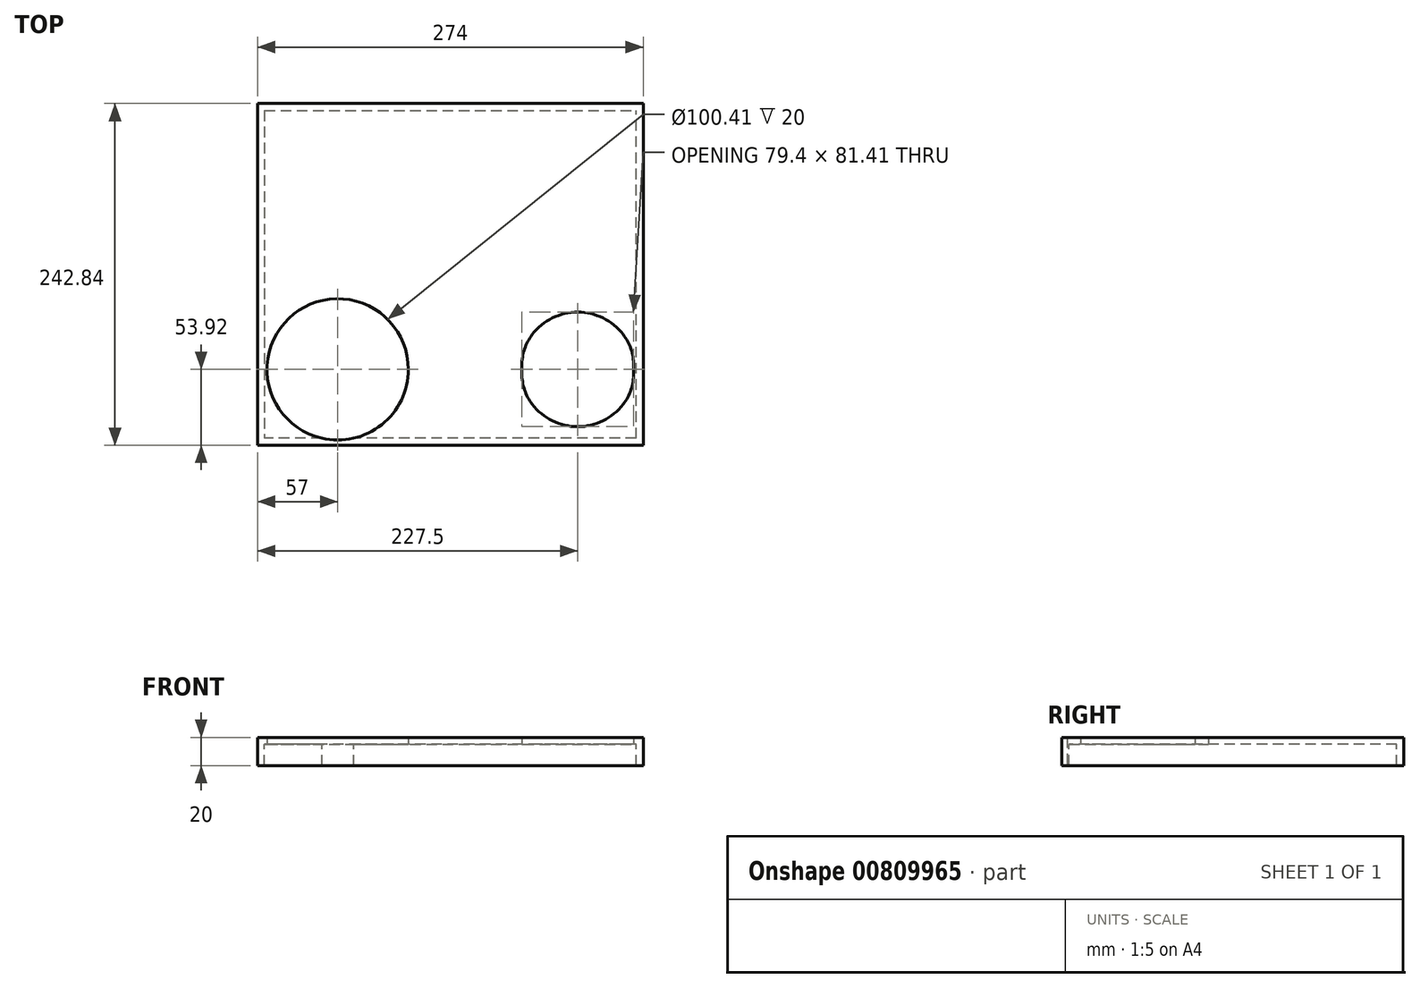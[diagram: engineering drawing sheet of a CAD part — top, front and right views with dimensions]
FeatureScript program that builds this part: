
annotation { "Feature Type Name" : "Feature", "Feature Type Description" : "" }
export const myFeature = defineFeature(function(context is Context, id is Id, definition is map)
    precondition{}
    {
        {
            var Q0;
            Q0=qCreatedBy(makeId("Top.planeOp"),FACE);
            var sketch = newSketch(context, id + "F0", { "sketchPlane" : qUnion([Q0])});
            skLineSegment(sketch, "E0", {"start": v(-69.05, 97.42) * mm, "end": v(-68.86, 97) * mm});
            skLineSegment(sketch, "E1", {"start": v(-70.25, 100) * mm, "end": v(-69.05, 97.42) * mm});
            skLineSegment(sketch, "E2", {"start": v(-70.71, 101) * mm, "end": v(-70.25, 100) * mm});
            skLineSegment(sketch, "E3", {"start": v(-75.98, 112.53) * mm, "end": v(-70.72, 101) * mm});
            skLineSegment(sketch, "E4", {"start": v(-75.97, 112.51) * mm, "end": v(-65.07, 114.65) * mm});
            skLineSegment(sketch, "E5", {"start": v(-65.07, 114.67) * mm, "end": v(-64.3, 114.83) * mm});
            skArc(sketch, "E6", {"start": v(-64.11, 114.85) * mm, "mid": v(-64.2, 114.84) * mm, "end": v(-64.3, 114.83) * mm});
            skLineSegment(sketch, "E7", {"start": v(-64.11, 114.85) * mm, "end": v(-62.9, 114.9) * mm});
            skLineSegment(sketch, "E8", {"start": v(139.49, -112.35) * mm, "end": v(140.85, -114.93) * mm});
            skLineSegment(sketch, "E9", {"start": v(139.48, -114.72) * mm, "end": v(140.85, -114.93) * mm});
            skLineSegment(sketch, "E10", {"start": v(130, -97.08) * mm, "end": v(130.29, -97.1) * mm});
            skLineSegment(sketch, "E11", {"start": v(130.29, -97.1) * mm, "end": v(131.36, -97) * mm});
            skLineSegment(sketch, "E12", {"start": v(131.36, -97.01) * mm, "end": v(132.95, -100) * mm});
            skLineSegment(sketch, "E13", {"start": v(132.95, -100) * mm, "end": v(133.48, -101) * mm});
            skLineSegment(sketch, "E14", {"start": v(133.48, -101) * mm, "end": v(139.49, -112.35) * mm});
            skLineSegment(sketch, "E15", {"start": v(136.64, -109.43) * mm, "end": v(139.48, -114.72) * mm});
            skLineSegment(sketch, "E16", {"start": v(139.48, -114.72) * mm, "end": v(-60.98, -114.72) * mm});
            skLineSegment(sketch, "E17", {"start": v(-51.5, -97.08) * mm, "end": v(130, -97.08) * mm});
            skLineSegment(sketch, "E18", {"start": v(130, -97.08) * mm, "end": v(131.57, -100) * mm});
            skLineSegment(sketch, "E19", {"start": v(131.57, -100) * mm, "end": v(132.1, -101) * mm});
            skLineSegment(sketch, "E20", {"start": v(132.1, -101) * mm, "end": v(136.64, -109.43) * mm});
            skLineSegment(sketch, "E21", {"start": v(-60.98, -114.72) * mm, "end": v(-58.14, -109.43) * mm});
            skLineSegment(sketch, "E22", {"start": v(-62.35, -114.94) * mm, "end": v(-60.98, -114.72) * mm});
            skLineSegment(sketch, "E23", {"start": v(-52.86, -97) * mm, "end": v(-51.79, -97.1) * mm});
            skLineSegment(sketch, "E24", {"start": v(-51.79, -97.1) * mm, "end": v(-51.5, -97.08) * mm});
            skLineSegment(sketch, "E25", {"start": v(-53.07, -100) * mm, "end": v(-51.5, -97.08) * mm});
            skLineSegment(sketch, "E26", {"start": v(-53.6, -101) * mm, "end": v(-53.07, -100) * mm});
            skLineSegment(sketch, "E27", {"start": v(-58.14, -109.43) * mm, "end": v(-53.6, -101) * mm});
            skLineSegment(sketch, "E28", {"start": v(-62.35, -114.93) * mm, "end": v(-60.99, -112.35) * mm});
            skLineSegment(sketch, "E29", {"start": v(-75.98, -112.53) * mm, "end": v(-70.72, -101) * mm});
            skLineSegment(sketch, "E30", {"start": v(-70.71, -101) * mm, "end": v(-70.25, -100) * mm});
            skLineSegment(sketch, "E31", {"start": v(-70.25, -100) * mm, "end": v(-69.05, -97.42) * mm});
            skLineSegment(sketch, "E32", {"start": v(-69.05, -97.42) * mm, "end": v(-68.86, -97) * mm});
            skLineSegment(sketch, "E33", {"start": v(-68.86, -97) * mm, "end": v(-68.39, -96) * mm});
            skLineSegment(sketch, "E34", {"start": v(-68.39, -96) * mm, "end": v(-67.71, -94.55) * mm});
            skLineSegment(sketch, "E35", {"start": v(-67.71, -94.56) * mm, "end": v(-59.49, -96.01) * mm});
            skLineSegment(sketch, "E36", {"start": v(-59.49, -96) * mm, "end": v(-56.67, -96.45) * mm});
            skLineSegment(sketch, "E37", {"start": v(-56.67, -96.46) * mm, "end": v(-52.94, -97) * mm});
            skLineSegment(sketch, "E38", {"start": v(-52.94, -97) * mm, "end": v(-52.86, -97.01) * mm});
            skLineSegment(sketch, "E39", {"start": v(-54.45, -100) * mm, "end": v(-52.86, -97.01) * mm});
            skLineSegment(sketch, "E40", {"start": v(-54.98, -101) * mm, "end": v(-54.45, -100) * mm});
            skLineSegment(sketch, "E41", {"start": v(-60.99, -112.35) * mm, "end": v(-54.98, -101) * mm});
            skLineSegment(sketch, "E42", {"start": v(-62.9, -114.9) * mm, "end": v(-62.35, -114.93) * mm});
            skLineSegment(sketch, "E43", {"start": v(-64.53, -115.5) * mm, "end": v(-62.85, -115.56) * mm});
            skLineSegment(sketch, "E44", {"start": v(-64.11, -114.85) * mm, "end": v(-62.9, -114.9) * mm});
            skArc(sketch, "E45", {"start": v(-64.88, -115.47) * mm, "mid": v(-64.7, -115.5) * mm, "end": v(-64.53, -115.5) * mm});
            skArc(sketch, "E46", {"start": v(-64.3, -114.83) * mm, "mid": v(-64.2, -114.84) * mm, "end": v(-64.11, -114.85) * mm});
            skLineSegment(sketch, "E47", {"start": v(-75.97, -112.51) * mm, "end": v(-65.07, -114.65) * mm});
            skLineSegment(sketch, "E48", {"start": v(-65.07, -114.67) * mm, "end": v(-64.3, -114.83) * mm});
            skLineSegment(sketch, "E49", {"start": v(-64.9, -115.47) * mm, "end": v(-64.88, -115.47) * mm});
            skLineSegment(sketch, "E50", {"start": v(-64.88, -115.47) * mm, "end": v(-64.92, -115.97) * mm});
            skLineSegment(sketch, "E51", {"start": v(-91.1, -111.35) * mm, "end": v(-64.92, -115.97) * mm});
            skLineSegment(sketch, "E52", {"start": v(-91.1, -111.35) * mm, "end": v(-90.57, -110.91) * mm});
            skLineSegment(sketch, "E53", {"start": v(-76.02, -113.37) * mm, "end": v(-66.82, -115.07) * mm});
            skLineSegment(sketch, "E54", {"start": v(-66.82, -115.08) * mm, "end": v(-64.9, -115.47) * mm});
            skLineSegment(sketch, "E55", {"start": v(157.61, -91.65) * mm, "end": v(130.3, -96.47) * mm});
            skLineSegment(sketch, "E56", {"start": v(130.3, -96.47) * mm, "end": v(-51.8, -96.47) * mm});
            skLineSegment(sketch, "E57", {"start": v(-51.8, -96.47) * mm, "end": v(-79.11, -91.65) * mm});
            skLineSegment(sketch, "E58", {"start": v(-79.53, -91.16) * mm, "end": v(-79.52, -91.23) * mm});
            skLineSegment(sketch, "E59", {"start": v(-79.52, -91.23) * mm, "end": v(-79.5, -91.3) * mm});
            skLineSegment(sketch, "E60", {"start": v(-79.5, -91.3) * mm, "end": v(-79.48, -91.37) * mm});
            skLineSegment(sketch, "E61", {"start": v(-79.48, -91.37) * mm, "end": v(-79.45, -91.43) * mm});
            skLineSegment(sketch, "E62", {"start": v(-79.45, -91.43) * mm, "end": v(-79.41, -91.48) * mm});
            skLineSegment(sketch, "E63", {"start": v(-79.41, -91.48) * mm, "end": v(-79.36, -91.53) * mm});
            skLineSegment(sketch, "E64", {"start": v(-79.36, -91.53) * mm, "end": v(-79.3, -91.58) * mm});
            skLineSegment(sketch, "E65", {"start": v(-79.3, -91.58) * mm, "end": v(-79.25, -91.61) * mm});
            skLineSegment(sketch, "E66", {"start": v(-79.25, -91.61) * mm, "end": v(-79.18, -91.64) * mm});
            skLineSegment(sketch, "E67", {"start": v(-79.18, -91.64) * mm, "end": v(-79.11, -91.65) * mm});
            skLineSegment(sketch, "E68", {"start": v(-79.53, -91.16) * mm, "end": v(-79.53, 91.16) * mm});
            skEllipticalArc(sketch, "E69", {});
            skLineSegment(sketch, "E70", {"start": v(-79.11, 91.65) * mm, "end": v(-51.8, 96.47) * mm});
            skLineSegment(sketch, "E71", {"start": v(-51.8, 96.47) * mm, "end": v(130.3, 96.47) * mm});
            skLineSegment(sketch, "E72", {"start": v(130.3, 96.47) * mm, "end": v(157.61, 91.65) * mm});
            skLineSegment(sketch, "E73", {"start": v(158.03, 91.16) * mm, "end": v(158.02, 91.23) * mm});
            skLineSegment(sketch, "E74", {"start": v(158.02, 91.23) * mm, "end": v(158, 91.3) * mm});
            skLineSegment(sketch, "E75", {"start": v(158, 91.3) * mm, "end": v(157.98, 91.37) * mm});
            skLineSegment(sketch, "E76", {"start": v(157.98, 91.37) * mm, "end": v(157.95, 91.43) * mm});
            skLineSegment(sketch, "E77", {"start": v(157.95, 91.43) * mm, "end": v(157.91, 91.48) * mm});
            skLineSegment(sketch, "E78", {"start": v(157.91, 91.48) * mm, "end": v(157.86, 91.53) * mm});
            skLineSegment(sketch, "E79", {"start": v(157.86, 91.53) * mm, "end": v(157.8, 91.58) * mm});
            skLineSegment(sketch, "E80", {"start": v(157.8, 91.58) * mm, "end": v(157.75, 91.61) * mm});
            skLineSegment(sketch, "E81", {"start": v(157.75, 91.61) * mm, "end": v(157.68, 91.64) * mm});
            skLineSegment(sketch, "E82", {"start": v(157.68, 91.64) * mm, "end": v(157.61, 91.65) * mm});
            skLineSegment(sketch, "E83", {"start": v(158.03, 91.16) * mm, "end": v(158.03, -91.16) * mm});
            skLineSegment(sketch, "E84", {"start": v(157.61, -91.65) * mm, "end": v(157.68, -91.64) * mm});
            skLineSegment(sketch, "E85", {"start": v(157.68, -91.64) * mm, "end": v(157.75, -91.61) * mm});
            skLineSegment(sketch, "E86", {"start": v(157.75, -91.61) * mm, "end": v(157.8, -91.58) * mm});
            skLineSegment(sketch, "E87", {"start": v(157.8, -91.58) * mm, "end": v(157.86, -91.53) * mm});
            skLineSegment(sketch, "E88", {"start": v(157.86, -91.53) * mm, "end": v(157.91, -91.48) * mm});
            skLineSegment(sketch, "E89", {"start": v(157.91, -91.48) * mm, "end": v(157.95, -91.43) * mm});
            skLineSegment(sketch, "E90", {"start": v(157.95, -91.43) * mm, "end": v(157.98, -91.37) * mm});
            skLineSegment(sketch, "E91", {"start": v(157.98, -91.37) * mm, "end": v(158, -91.3) * mm});
            skLineSegment(sketch, "E92", {"start": v(158, -91.3) * mm, "end": v(158.02, -91.23) * mm});
            skLineSegment(sketch, "E93", {"start": v(158.02, -91.23) * mm, "end": v(158.03, -91.16) * mm});
            skLineSegment(sketch, "E94", {"start": v(169.07, -110.91) * mm, "end": v(169.09, -110.9) * mm});
            skLineSegment(sketch, "E95", {"start": v(169.09, -110.9) * mm, "end": v(169.1, -110.86) * mm});
            skLineSegment(sketch, "E96", {"start": v(169.1, -110.86) * mm, "end": v(169.1, -110.8) * mm});
            skLineSegment(sketch, "E97", {"start": v(169.1, -110.8) * mm, "end": v(169.1, -110.73) * mm});
            skLineSegment(sketch, "E98", {"start": v(169.1, -110.73) * mm, "end": v(169.1, -110.64) * mm});
            skLineSegment(sketch, "E99", {"start": v(169.1, -110.64) * mm, "end": v(169.1, -110.54) * mm});
            skLineSegment(sketch, "E100", {"start": v(169.1, -110.54) * mm, "end": v(169.1, -110.43) * mm});
            skLineSegment(sketch, "E101", {"start": v(169.1, -110.43) * mm, "end": v(169.08, -110.31) * mm});
            skLineSegment(sketch, "E102", {"start": v(169.08, -110.31) * mm, "end": v(169.06, -110.18) * mm});
            skLineSegment(sketch, "E103", {"start": v(169.06, -110.18) * mm, "end": v(169.04, -110.05) * mm});
            skEllipticalArc(sketch, "E104", {});
            skLineSegment(sketch, "E105", {"start": v(142.98, -115.5) * mm, "end": v(143.03, -115.5) * mm});
            skLineSegment(sketch, "E106", {"start": v(142.61, -114.85) * mm, "end": v(142.64, -114.97) * mm});
            skLineSegment(sketch, "E107", {"start": v(142.64, -114.97) * mm, "end": v(142.67, -115.09) * mm});
            skLineSegment(sketch, "E108", {"start": v(142.67, -115.09) * mm, "end": v(142.71, -115.19) * mm});
            skLineSegment(sketch, "E109", {"start": v(142.71, -115.19) * mm, "end": v(142.76, -115.28) * mm});
            skLineSegment(sketch, "E110", {"start": v(142.76, -115.28) * mm, "end": v(142.8, -115.36) * mm});
            skLineSegment(sketch, "E111", {"start": v(142.8, -115.36) * mm, "end": v(142.86, -115.42) * mm});
            skLineSegment(sketch, "E112", {"start": v(142.86, -115.42) * mm, "end": v(142.92, -115.47) * mm});
            skLineSegment(sketch, "E113", {"start": v(142.92, -115.47) * mm, "end": v(142.98, -115.5) * mm});
            skEllipticalArc(sketch, "E114", {});
            skLineSegment(sketch, "E115", {"start": v(140.85, -114.93) * mm, "end": v(140.89, -115.06) * mm});
            skLineSegment(sketch, "E116", {"start": v(140.89, -115.06) * mm, "end": v(140.93, -115.18) * mm});
            skLineSegment(sketch, "E117", {"start": v(140.93, -115.18) * mm, "end": v(140.99, -115.28) * mm});
            skLineSegment(sketch, "E118", {"start": v(140.99, -115.28) * mm, "end": v(141.05, -115.37) * mm});
            skLineSegment(sketch, "E119", {"start": v(141.05, -115.37) * mm, "end": v(141.12, -115.45) * mm});
            skLineSegment(sketch, "E120", {"start": v(141.12, -115.45) * mm, "end": v(141.2, -115.5) * mm});
            skLineSegment(sketch, "E121", {"start": v(141.2, -115.5) * mm, "end": v(141.27, -115.54) * mm});
            skLineSegment(sketch, "E122", {"start": v(141.27, -115.54) * mm, "end": v(141.35, -115.56) * mm});
            skLineSegment(sketch, "E123", {"start": v(169.04, 110.05) * mm, "end": v(169.06, 110.18) * mm});
            skLineSegment(sketch, "E124", {"start": v(169.06, 110.18) * mm, "end": v(169.08, 110.31) * mm});
            skLineSegment(sketch, "E125", {"start": v(169.08, 110.31) * mm, "end": v(169.1, 110.43) * mm});
            skLineSegment(sketch, "E126", {"start": v(169.1, 110.43) * mm, "end": v(169.1, 110.54) * mm});
            skLineSegment(sketch, "E127", {"start": v(169.1, 110.54) * mm, "end": v(169.1, 110.64) * mm});
            skLineSegment(sketch, "E128", {"start": v(169.1, 110.64) * mm, "end": v(169.1, 110.73) * mm});
            skLineSegment(sketch, "E129", {"start": v(169.1, 110.73) * mm, "end": v(169.1, 110.8) * mm});
            skLineSegment(sketch, "E130", {"start": v(169.1, 110.8) * mm, "end": v(169.1, 110.86) * mm});
            skLineSegment(sketch, "E131", {"start": v(169.1, 110.86) * mm, "end": v(169.09, 110.9) * mm});
            skLineSegment(sketch, "E132", {"start": v(169.09, 110.9) * mm, "end": v(169.07, 110.91) * mm});
            skLineSegment(sketch, "E133", {"start": v(139.48, -114.72) * mm, "end": v(139.48, -115.59) * mm});
            skLineSegment(sketch, "E134", {"start": v(-60.98, -114.72) * mm, "end": v(-60.98, -115.59) * mm});
            skEllipticalArc(sketch, "E135", {});
            skEllipticalArc(sketch, "E136", {});
            skEllipticalArc(sketch, "E137", {});
            skLineSegment(sketch, "E138", {"start": v(139.48, 115.59) * mm, "end": v(139.48, 114.72) * mm});
            skLineSegment(sketch, "E139", {"start": v(-60.98, 115.59) * mm, "end": v(-60.98, 114.72) * mm});
            skLineSegment(sketch, "E140", {"start": v(-90.54, -110.05) * mm, "end": v(-90.56, -110.18) * mm});
            skLineSegment(sketch, "E141", {"start": v(-90.56, -110.18) * mm, "end": v(-90.58, -110.31) * mm});
            skLineSegment(sketch, "E142", {"start": v(-90.58, -110.31) * mm, "end": v(-90.6, -110.43) * mm});
            skLineSegment(sketch, "E143", {"start": v(-90.6, -110.43) * mm, "end": v(-90.6, -110.54) * mm});
            skLineSegment(sketch, "E144", {"start": v(-90.6, -110.54) * mm, "end": v(-90.6, -110.64) * mm});
            skLineSegment(sketch, "E145", {"start": v(-90.6, -110.64) * mm, "end": v(-90.6, -110.73) * mm});
            skLineSegment(sketch, "E146", {"start": v(-90.6, -110.73) * mm, "end": v(-90.6, -110.8) * mm});
            skLineSegment(sketch, "E147", {"start": v(-90.6, -110.8) * mm, "end": v(-90.6, -110.86) * mm});
            skLineSegment(sketch, "E148", {"start": v(-90.6, -110.86) * mm, "end": v(-90.59, -110.9) * mm});
            skLineSegment(sketch, "E149", {"start": v(-90.59, -110.9) * mm, "end": v(-90.57, -110.91) * mm});
            skLineSegment(sketch, "E150", {"start": v(-92.22, -108.95) * mm, "end": v(-92.2, -108.96) * mm});
            skLineSegment(sketch, "E151", {"start": v(-92.2, -108.96) * mm, "end": v(-92.17, -108.98) * mm});
            skLineSegment(sketch, "E152", {"start": v(-92.17, -108.98) * mm, "end": v(-92.12, -109) * mm});
            skLineSegment(sketch, "E153", {"start": v(-92.12, -109) * mm, "end": v(-92.05, -109.01) * mm});
            skLineSegment(sketch, "E154", {"start": v(-92.05, -109.01) * mm, "end": v(-91.96, -109.02) * mm});
            skLineSegment(sketch, "E155", {"start": v(-91.96, -109.02) * mm, "end": v(-91.87, -109.04) * mm});
            skLineSegment(sketch, "E156", {"start": v(-91.87, -109.04) * mm, "end": v(-91.75, -109.05) * mm});
            skLineSegment(sketch, "E157", {"start": v(-91.75, -109.05) * mm, "end": v(-91.63, -109.06) * mm});
            skLineSegment(sketch, "E158", {"start": v(-91.63, -109.06) * mm, "end": v(-91.5, -109.06) * mm});
            skLineSegment(sketch, "E159", {"start": v(-91.5, -109.06) * mm, "end": v(-91.37, -109.07) * mm});
            skEllipticalArc(sketch, "E160", {});
            skEllipticalArc(sketch, "E161", {});
            skLineSegment(sketch, "E162", {"start": v(158.4, -92.33) * mm, "end": v(158.39, -92.26) * mm});
            skLineSegment(sketch, "E163", {"start": v(158.39, -92.26) * mm, "end": v(158.38, -92.2) * mm});
            skLineSegment(sketch, "E164", {"start": v(158.38, -92.2) * mm, "end": v(158.36, -92.13) * mm});
            skLineSegment(sketch, "E165", {"start": v(158.36, -92.13) * mm, "end": v(158.35, -92.06) * mm});
            skLineSegment(sketch, "E166", {"start": v(158.35, -92.06) * mm, "end": v(158.33, -92) * mm});
            skLineSegment(sketch, "E167", {"start": v(158.33, -92) * mm, "end": v(158.32, -91.95) * mm});
            skLineSegment(sketch, "E168", {"start": v(158.32, -91.95) * mm, "end": v(158.3, -91.9) * mm});
            skLineSegment(sketch, "E169", {"start": v(158.3, -91.9) * mm, "end": v(158.3, -91.86) * mm});
            skLineSegment(sketch, "E170", {"start": v(158.3, -91.86) * mm, "end": v(158.28, -91.83) * mm});
            skLineSegment(sketch, "E171", {"start": v(158.28, -91.83) * mm, "end": v(158.27, -91.8) * mm});
            skLineSegment(sketch, "E172", {"start": v(158.27, -91.8) * mm, "end": v(158.26, -91.79) * mm});
            skLineSegment(sketch, "E173", {"start": v(158.26, -91.79) * mm, "end": v(158.25, -91.78) * mm});
            skLineSegment(sketch, "E174", {"start": v(158.67, -91.3) * mm, "end": v(158.68, -91.3) * mm});
            skLineSegment(sketch, "E175", {"start": v(158.68, -91.3) * mm, "end": v(158.7, -91.3) * mm});
            skLineSegment(sketch, "E176", {"start": v(158.7, -91.3) * mm, "end": v(158.74, -91.31) * mm});
            skLineSegment(sketch, "E177", {"start": v(158.74, -91.31) * mm, "end": v(158.78, -91.32) * mm});
            skLineSegment(sketch, "E178", {"start": v(158.78, -91.32) * mm, "end": v(158.83, -91.33) * mm});
            skLineSegment(sketch, "E179", {"start": v(158.83, -91.33) * mm, "end": v(158.89, -91.33) * mm});
            skLineSegment(sketch, "E180", {"start": v(158.89, -91.33) * mm, "end": v(158.95, -91.34) * mm});
            skLineSegment(sketch, "E181", {"start": v(158.95, -91.34) * mm, "end": v(159.02, -91.34) * mm});
            skLineSegment(sketch, "E182", {"start": v(159.02, -91.34) * mm, "end": v(159.09, -91.34) * mm});
            skLineSegment(sketch, "E183", {"start": v(159.09, -91.34) * mm, "end": v(159.16, -91.34) * mm});
            skLineSegment(sketch, "E184", {"start": v(159.16, -91.34) * mm, "end": v(159.23, -91.34) * mm});
            skEllipticalArc(sketch, "E185", {});
            skLineSegment(sketch, "E186", {"start": v(158.25, 91.78) * mm, "end": v(158.26, 91.79) * mm});
            skLineSegment(sketch, "E187", {"start": v(158.26, 91.79) * mm, "end": v(158.27, 91.8) * mm});
            skLineSegment(sketch, "E188", {"start": v(158.27, 91.8) * mm, "end": v(158.28, 91.83) * mm});
            skLineSegment(sketch, "E189", {"start": v(158.28, 91.83) * mm, "end": v(158.3, 91.86) * mm});
            skLineSegment(sketch, "E190", {"start": v(158.3, 91.86) * mm, "end": v(158.3, 91.9) * mm});
            skLineSegment(sketch, "E191", {"start": v(158.3, 91.9) * mm, "end": v(158.32, 91.95) * mm});
            skLineSegment(sketch, "E192", {"start": v(158.32, 91.95) * mm, "end": v(158.33, 92) * mm});
            skLineSegment(sketch, "E193", {"start": v(158.33, 92) * mm, "end": v(158.35, 92.06) * mm});
            skLineSegment(sketch, "E194", {"start": v(158.35, 92.06) * mm, "end": v(158.36, 92.13) * mm});
            skLineSegment(sketch, "E195", {"start": v(158.36, 92.13) * mm, "end": v(158.38, 92.2) * mm});
            skLineSegment(sketch, "E196", {"start": v(158.38, 92.2) * mm, "end": v(158.39, 92.26) * mm});
            skLineSegment(sketch, "E197", {"start": v(158.39, 92.26) * mm, "end": v(158.4, 92.33) * mm});
            skLineSegment(sketch, "E198", {"start": v(-79.75, -91.78) * mm, "end": v(-79.76, -91.79) * mm});
            skLineSegment(sketch, "E199", {"start": v(-79.76, -91.79) * mm, "end": v(-79.77, -91.8) * mm});
            skLineSegment(sketch, "E200", {"start": v(-79.77, -91.8) * mm, "end": v(-79.78, -91.83) * mm});
            skLineSegment(sketch, "E201", {"start": v(-79.78, -91.83) * mm, "end": v(-79.8, -91.86) * mm});
            skLineSegment(sketch, "E202", {"start": v(-79.8, -91.86) * mm, "end": v(-79.8, -91.9) * mm});
            skLineSegment(sketch, "E203", {"start": v(-79.8, -91.9) * mm, "end": v(-79.82, -91.95) * mm});
            skLineSegment(sketch, "E204", {"start": v(-79.82, -91.95) * mm, "end": v(-79.83, -92) * mm});
            skLineSegment(sketch, "E205", {"start": v(-79.83, -92) * mm, "end": v(-79.85, -92.06) * mm});
            skLineSegment(sketch, "E206", {"start": v(-79.85, -92.06) * mm, "end": v(-79.86, -92.13) * mm});
            skLineSegment(sketch, "E207", {"start": v(-79.86, -92.13) * mm, "end": v(-79.88, -92.2) * mm});
            skLineSegment(sketch, "E208", {"start": v(-79.88, -92.2) * mm, "end": v(-79.89, -92.26) * mm});
            skLineSegment(sketch, "E209", {"start": v(-79.89, -92.26) * mm, "end": v(-79.9, -92.33) * mm});
            skLineSegment(sketch, "E210", {"start": v(-80.73, -91.34) * mm, "end": v(-80.66, -91.34) * mm});
            skLineSegment(sketch, "E211", {"start": v(-80.66, -91.34) * mm, "end": v(-80.59, -91.34) * mm});
            skLineSegment(sketch, "E212", {"start": v(-80.59, -91.34) * mm, "end": v(-80.52, -91.34) * mm});
            skLineSegment(sketch, "E213", {"start": v(-80.52, -91.34) * mm, "end": v(-80.45, -91.34) * mm});
            skLineSegment(sketch, "E214", {"start": v(-80.45, -91.34) * mm, "end": v(-80.39, -91.33) * mm});
            skLineSegment(sketch, "E215", {"start": v(-80.39, -91.33) * mm, "end": v(-80.33, -91.33) * mm});
            skLineSegment(sketch, "E216", {"start": v(-80.33, -91.33) * mm, "end": v(-80.28, -91.32) * mm});
            skLineSegment(sketch, "E217", {"start": v(-80.28, -91.32) * mm, "end": v(-80.24, -91.31) * mm});
            skLineSegment(sketch, "E218", {"start": v(-80.24, -91.31) * mm, "end": v(-80.2, -91.3) * mm});
            skLineSegment(sketch, "E219", {"start": v(-80.2, -91.3) * mm, "end": v(-80.18, -91.3) * mm});
            skLineSegment(sketch, "E220", {"start": v(-80.18, -91.3) * mm, "end": v(-80.17, -91.3) * mm});
            skLineSegment(sketch, "E221", {"start": v(-80.17, 91.3) * mm, "end": v(-80.18, 91.3) * mm});
            skLineSegment(sketch, "E222", {"start": v(-80.18, 91.3) * mm, "end": v(-80.2, 91.3) * mm});
            skLineSegment(sketch, "E223", {"start": v(-80.2, 91.3) * mm, "end": v(-80.24, 91.31) * mm});
            skLineSegment(sketch, "E224", {"start": v(-80.24, 91.31) * mm, "end": v(-80.28, 91.32) * mm});
            skLineSegment(sketch, "E225", {"start": v(-80.28, 91.32) * mm, "end": v(-80.33, 91.33) * mm});
            skLineSegment(sketch, "E226", {"start": v(-80.33, 91.33) * mm, "end": v(-80.39, 91.33) * mm});
            skLineSegment(sketch, "E227", {"start": v(-80.39, 91.33) * mm, "end": v(-80.45, 91.34) * mm});
            skLineSegment(sketch, "E228", {"start": v(-80.45, 91.34) * mm, "end": v(-80.52, 91.34) * mm});
            skLineSegment(sketch, "E229", {"start": v(-80.52, 91.34) * mm, "end": v(-80.59, 91.34) * mm});
            skLineSegment(sketch, "E230", {"start": v(-80.59, 91.34) * mm, "end": v(-80.66, 91.34) * mm});
            skLineSegment(sketch, "E231", {"start": v(-80.66, 91.34) * mm, "end": v(-80.73, 91.34) * mm});
            skLineSegment(sketch, "E232", {"start": v(-79.9, 92.33) * mm, "end": v(-79.89, 92.26) * mm});
            skLineSegment(sketch, "E233", {"start": v(-79.89, 92.26) * mm, "end": v(-79.88, 92.2) * mm});
            skLineSegment(sketch, "E234", {"start": v(-79.88, 92.2) * mm, "end": v(-79.86, 92.13) * mm});
            skLineSegment(sketch, "E235", {"start": v(-79.86, 92.13) * mm, "end": v(-79.85, 92.06) * mm});
            skLineSegment(sketch, "E236", {"start": v(-79.85, 92.06) * mm, "end": v(-79.83, 92) * mm});
            skLineSegment(sketch, "E237", {"start": v(-79.83, 92) * mm, "end": v(-79.82, 91.95) * mm});
            skLineSegment(sketch, "E238", {"start": v(-79.82, 91.95) * mm, "end": v(-79.8, 91.9) * mm});
            skLineSegment(sketch, "E239", {"start": v(-79.8, 91.9) * mm, "end": v(-79.8, 91.86) * mm});
            skLineSegment(sketch, "E240", {"start": v(-79.8, 91.86) * mm, "end": v(-79.78, 91.83) * mm});
            skLineSegment(sketch, "E241", {"start": v(-79.78, 91.83) * mm, "end": v(-79.77, 91.8) * mm});
            skLineSegment(sketch, "E242", {"start": v(-79.77, 91.8) * mm, "end": v(-79.76, 91.79) * mm});
            skLineSegment(sketch, "E243", {"start": v(-79.76, 91.79) * mm, "end": v(-79.75, 91.78) * mm});
            skLineSegment(sketch, "E244", {"start": v(-51.5, -96.52) * mm, "end": v(-51.5, -97) * mm});
            skLineSegment(sketch, "E245", {"start": v(-51.5, -97) * mm, "end": v(-51.5, -97.08) * mm});
            skLineSegment(sketch, "E246", {"start": v(130, -96.52) * mm, "end": v(130, -97) * mm});
            skLineSegment(sketch, "E247", {"start": v(130, -97) * mm, "end": v(130, -97.08) * mm});
            skLineSegment(sketch, "E248", {"start": v(130, 97.08) * mm, "end": v(130, 97) * mm});
            skLineSegment(sketch, "E249", {"start": v(130, 97) * mm, "end": v(130, 96.52) * mm});
            skLineSegment(sketch, "E250", {"start": v(-51.5, 97) * mm, "end": v(-51.5, 96.52) * mm});
            skLineSegment(sketch, "E251", {"start": v(-51.5, 97.08) * mm, "end": v(-51.5, 97) * mm});
            skEllipticalArc(sketch, "E252", {});
            skEllipticalArc(sketch, "E253", {});
            skLineSegment(sketch, "E254", {"start": v(-90.54, 110.05) * mm, "end": v(-75.97, 112.53) * mm});
            skLineSegment(sketch, "E255", {"start": v(-67.71, 94.55) * mm, "end": v(-79.9, 92.33) * mm});
            skEllipticalArc(sketch, "E256", {});
            skEllipticalArc(sketch, "E257", {});
            skLineSegment(sketch, "E258", {"start": v(146.21, -94.55) * mm, "end": v(146.2, -94.48) * mm});
            skLineSegment(sketch, "E259", {"start": v(146.2, -94.48) * mm, "end": v(146.19, -94.41) * mm});
            skLineSegment(sketch, "E260", {"start": v(146.19, -94.41) * mm, "end": v(146.17, -94.35) * mm});
            skLineSegment(sketch, "E261", {"start": v(146.17, -94.35) * mm, "end": v(146.16, -94.28) * mm});
            skLineSegment(sketch, "E262", {"start": v(146.16, -94.28) * mm, "end": v(146.14, -94.22) * mm});
            skLineSegment(sketch, "E263", {"start": v(146.14, -94.22) * mm, "end": v(146.13, -94.17) * mm});
            skLineSegment(sketch, "E264", {"start": v(146.13, -94.17) * mm, "end": v(146.12, -94.12) * mm});
            skLineSegment(sketch, "E265", {"start": v(146.12, -94.12) * mm, "end": v(146.1, -94.08) * mm});
            skLineSegment(sketch, "E266", {"start": v(146.1, -94.08) * mm, "end": v(146.1, -94.05) * mm});
            skLineSegment(sketch, "E267", {"start": v(146.1, -94.05) * mm, "end": v(146.08, -94.02) * mm});
            skLineSegment(sketch, "E268", {"start": v(146.08, -94.02) * mm, "end": v(146.07, -94) * mm});
            skLineSegment(sketch, "E269", {"start": v(146.07, -94) * mm, "end": v(146.06, -94) * mm});
            skLineSegment(sketch, "E270", {"start": v(131.36, -97) * mm, "end": v(131.36, -97.01) * mm});
            skLineSegment(sketch, "E271", {"start": v(131.55, -96.33) * mm, "end": v(131.51, -96.35) * mm});
            skLineSegment(sketch, "E272", {"start": v(131.51, -96.35) * mm, "end": v(131.47, -96.37) * mm});
            skLineSegment(sketch, "E273", {"start": v(131.47, -96.37) * mm, "end": v(131.44, -96.4) * mm});
            skLineSegment(sketch, "E274", {"start": v(131.44, -96.4) * mm, "end": v(131.4, -96.44) * mm});
            skLineSegment(sketch, "E275", {"start": v(131.4, -96.44) * mm, "end": v(131.38, -96.5) * mm});
            skLineSegment(sketch, "E276", {"start": v(131.38, -96.5) * mm, "end": v(131.36, -96.54) * mm});
            skLineSegment(sketch, "E277", {"start": v(131.36, -96.54) * mm, "end": v(131.34, -96.6) * mm});
            skLineSegment(sketch, "E278", {"start": v(131.34, -96.6) * mm, "end": v(131.33, -96.67) * mm});
            skLineSegment(sketch, "E279", {"start": v(131.33, -96.67) * mm, "end": v(131.32, -96.73) * mm});
            skLineSegment(sketch, "E280", {"start": v(131.32, -96.73) * mm, "end": v(131.32, -96.8) * mm});
            skLineSegment(sketch, "E281", {"start": v(131.32, -96.8) * mm, "end": v(131.33, -96.87) * mm});
            skLineSegment(sketch, "E282", {"start": v(131.33, -96.87) * mm, "end": v(131.34, -96.94) * mm});
            skLineSegment(sketch, "E283", {"start": v(131.34, -96.94) * mm, "end": v(131.36, -97) * mm});
            skLineSegment(sketch, "E284", {"start": v(-67.71, 94.55) * mm, "end": v(-67.7, 94.48) * mm});
            skLineSegment(sketch, "E285", {"start": v(-67.7, 94.48) * mm, "end": v(-67.69, 94.41) * mm});
            skLineSegment(sketch, "E286", {"start": v(-67.69, 94.41) * mm, "end": v(-67.67, 94.35) * mm});
            skLineSegment(sketch, "E287", {"start": v(-67.67, 94.35) * mm, "end": v(-67.66, 94.28) * mm});
            skLineSegment(sketch, "E288", {"start": v(-67.66, 94.28) * mm, "end": v(-67.64, 94.22) * mm});
            skLineSegment(sketch, "E289", {"start": v(-67.64, 94.22) * mm, "end": v(-67.63, 94.17) * mm});
            skLineSegment(sketch, "E290", {"start": v(-67.63, 94.17) * mm, "end": v(-67.62, 94.12) * mm});
            skLineSegment(sketch, "E291", {"start": v(-67.62, 94.12) * mm, "end": v(-67.6, 94.08) * mm});
            skLineSegment(sketch, "E292", {"start": v(-67.6, 94.08) * mm, "end": v(-67.6, 94.05) * mm});
            skLineSegment(sketch, "E293", {"start": v(-67.6, 94.05) * mm, "end": v(-67.58, 94.02) * mm});
            skLineSegment(sketch, "E294", {"start": v(-67.58, 94.02) * mm, "end": v(-67.57, 94) * mm});
            skLineSegment(sketch, "E295", {"start": v(-67.57, 94) * mm, "end": v(-67.56, 94) * mm});
            skLineSegment(sketch, "E296", {"start": v(-52.86, 97) * mm, "end": v(-52.86, 97.01) * mm});
            skEllipticalArc(sketch, "E297", {});
            skLineSegment(sketch, "E298", {"start": v(146.06, 94) * mm, "end": v(146.07, 94) * mm});
            skLineSegment(sketch, "E299", {"start": v(146.07, 94) * mm, "end": v(146.08, 94.02) * mm});
            skLineSegment(sketch, "E300", {"start": v(146.08, 94.02) * mm, "end": v(146.1, 94.05) * mm});
            skLineSegment(sketch, "E301", {"start": v(146.1, 94.05) * mm, "end": v(146.1, 94.08) * mm});
            skLineSegment(sketch, "E302", {"start": v(146.1, 94.08) * mm, "end": v(146.12, 94.12) * mm});
            skLineSegment(sketch, "E303", {"start": v(146.12, 94.12) * mm, "end": v(146.13, 94.17) * mm});
            skLineSegment(sketch, "E304", {"start": v(146.13, 94.17) * mm, "end": v(146.14, 94.22) * mm});
            skLineSegment(sketch, "E305", {"start": v(146.14, 94.22) * mm, "end": v(146.16, 94.28) * mm});
            skLineSegment(sketch, "E306", {"start": v(146.16, 94.28) * mm, "end": v(146.17, 94.35) * mm});
            skLineSegment(sketch, "E307", {"start": v(146.17, 94.35) * mm, "end": v(146.19, 94.41) * mm});
            skLineSegment(sketch, "E308", {"start": v(146.19, 94.41) * mm, "end": v(146.2, 94.48) * mm});
            skLineSegment(sketch, "E309", {"start": v(146.2, 94.48) * mm, "end": v(146.21, 94.55) * mm});
            skEllipticalArc(sketch, "E310", {});
            skLineSegment(sketch, "E311", {"start": v(131.36, 97.01) * mm, "end": v(131.36, 97) * mm});
            skLineSegment(sketch, "E312", {"start": v(-67.56, -94) * mm, "end": v(-67.57, -94) * mm});
            skLineSegment(sketch, "E313", {"start": v(-67.57, -94) * mm, "end": v(-67.58, -94.02) * mm});
            skLineSegment(sketch, "E314", {"start": v(-67.58, -94.02) * mm, "end": v(-67.6, -94.05) * mm});
            skLineSegment(sketch, "E315", {"start": v(-67.6, -94.05) * mm, "end": v(-67.6, -94.08) * mm});
            skLineSegment(sketch, "E316", {"start": v(-67.6, -94.08) * mm, "end": v(-67.62, -94.12) * mm});
            skLineSegment(sketch, "E317", {"start": v(-67.62, -94.12) * mm, "end": v(-67.63, -94.17) * mm});
            skLineSegment(sketch, "E318", {"start": v(-67.63, -94.17) * mm, "end": v(-67.64, -94.22) * mm});
            skLineSegment(sketch, "E319", {"start": v(-67.64, -94.22) * mm, "end": v(-67.66, -94.28) * mm});
            skLineSegment(sketch, "E320", {"start": v(-67.66, -94.28) * mm, "end": v(-67.67, -94.35) * mm});
            skLineSegment(sketch, "E321", {"start": v(-67.67, -94.35) * mm, "end": v(-67.69, -94.41) * mm});
            skLineSegment(sketch, "E322", {"start": v(-67.69, -94.41) * mm, "end": v(-67.7, -94.48) * mm});
            skLineSegment(sketch, "E323", {"start": v(-67.7, -94.48) * mm, "end": v(-67.71, -94.55) * mm});
            skLineSegment(sketch, "E324", {"start": v(-52.86, -97) * mm, "end": v(-52.84, -96.94) * mm});
            skLineSegment(sketch, "E325", {"start": v(-52.84, -96.94) * mm, "end": v(-52.83, -96.87) * mm});
            skLineSegment(sketch, "E326", {"start": v(-52.83, -96.87) * mm, "end": v(-52.82, -96.8) * mm});
            skLineSegment(sketch, "E327", {"start": v(-52.82, -96.8) * mm, "end": v(-52.82, -96.73) * mm});
            skLineSegment(sketch, "E328", {"start": v(-52.82, -96.73) * mm, "end": v(-52.83, -96.67) * mm});
            skLineSegment(sketch, "E329", {"start": v(-52.83, -96.67) * mm, "end": v(-52.84, -96.6) * mm});
            skLineSegment(sketch, "E330", {"start": v(-52.84, -96.6) * mm, "end": v(-52.86, -96.54) * mm});
            skLineSegment(sketch, "E331", {"start": v(-52.86, -96.54) * mm, "end": v(-52.88, -96.5) * mm});
            skLineSegment(sketch, "E332", {"start": v(-52.88, -96.5) * mm, "end": v(-52.9, -96.44) * mm});
            skLineSegment(sketch, "E333", {"start": v(-52.9, -96.44) * mm, "end": v(-52.94, -96.4) * mm});
            skLineSegment(sketch, "E334", {"start": v(-52.94, -96.4) * mm, "end": v(-52.97, -96.37) * mm});
            skLineSegment(sketch, "E335", {"start": v(-52.97, -96.37) * mm, "end": v(-53.01, -96.35) * mm});
            skLineSegment(sketch, "E336", {"start": v(-53.01, -96.35) * mm, "end": v(-53.05, -96.33) * mm});
            skLineSegment(sketch, "E337", {"start": v(-52.86, -97.01) * mm, "end": v(-52.86, -97) * mm});
            skLineSegment(sketch, "E338", {"start": v(143.37, -115.47) * mm, "end": v(143.38, -115.47) * mm});
            skLineSegment(sketch, "E339", {"start": v(142.8, -114.83) * mm, "end": v(142.84, -114.95) * mm});
            skLineSegment(sketch, "E340", {"start": v(142.84, -114.95) * mm, "end": v(142.9, -115.07) * mm});
            skLineSegment(sketch, "E341", {"start": v(142.9, -115.07) * mm, "end": v(142.96, -115.17) * mm});
            skLineSegment(sketch, "E342", {"start": v(142.96, -115.17) * mm, "end": v(143.02, -115.26) * mm});
            skLineSegment(sketch, "E343", {"start": v(143.02, -115.26) * mm, "end": v(143.1, -115.34) * mm});
            skLineSegment(sketch, "E344", {"start": v(143.1, -115.34) * mm, "end": v(143.16, -115.4) * mm});
            skLineSegment(sketch, "E345", {"start": v(143.16, -115.4) * mm, "end": v(143.23, -115.44) * mm});
            skLineSegment(sketch, "E346", {"start": v(143.23, -115.44) * mm, "end": v(143.3, -115.47) * mm});
            skLineSegment(sketch, "E347", {"start": v(143.3, -115.47) * mm, "end": v(143.37, -115.47) * mm});
            skLineSegment(sketch, "E348", {"start": v(154.52, -113.39) * mm, "end": v(154.53, -113.37) * mm});
            skLineSegment(sketch, "E349", {"start": v(154.53, -113.37) * mm, "end": v(154.54, -113.33) * mm});
            skLineSegment(sketch, "E350", {"start": v(154.54, -113.33) * mm, "end": v(154.54, -113.28) * mm});
            skLineSegment(sketch, "E351", {"start": v(154.54, -113.28) * mm, "end": v(154.54, -113.2) * mm});
            skLineSegment(sketch, "E352", {"start": v(154.54, -113.2) * mm, "end": v(154.54, -113.12) * mm});
            skLineSegment(sketch, "E353", {"start": v(154.54, -113.12) * mm, "end": v(154.53, -113.02) * mm});
            skLineSegment(sketch, "E354", {"start": v(154.53, -113.02) * mm, "end": v(154.52, -112.91) * mm});
            skLineSegment(sketch, "E355", {"start": v(154.52, -112.91) * mm, "end": v(154.5, -112.8) * mm});
            skLineSegment(sketch, "E356", {"start": v(154.5, -112.8) * mm, "end": v(154.5, -112.66) * mm});
            skLineSegment(sketch, "E357", {"start": v(154.5, -112.66) * mm, "end": v(154.47, -112.53) * mm});
            skLineSegment(sketch, "E358", {"start": v(143.38, 115.47) * mm, "end": v(143.37, 115.47) * mm});
            skLineSegment(sketch, "E359", {"start": v(154.47, 112.53) * mm, "end": v(154.5, 112.66) * mm});
            skLineSegment(sketch, "E360", {"start": v(154.5, 112.66) * mm, "end": v(154.5, 112.8) * mm});
            skLineSegment(sketch, "E361", {"start": v(154.5, 112.8) * mm, "end": v(154.52, 112.91) * mm});
            skLineSegment(sketch, "E362", {"start": v(154.52, 112.91) * mm, "end": v(154.53, 113.02) * mm});
            skLineSegment(sketch, "E363", {"start": v(154.53, 113.02) * mm, "end": v(154.54, 113.12) * mm});
            skLineSegment(sketch, "E364", {"start": v(154.54, 113.12) * mm, "end": v(154.54, 113.2) * mm});
            skLineSegment(sketch, "E365", {"start": v(154.54, 113.2) * mm, "end": v(154.54, 113.28) * mm});
            skLineSegment(sketch, "E366", {"start": v(154.54, 113.28) * mm, "end": v(154.54, 113.33) * mm});
            skLineSegment(sketch, "E367", {"start": v(154.54, 113.33) * mm, "end": v(154.53, 113.37) * mm});
            skLineSegment(sketch, "E368", {"start": v(154.53, 113.37) * mm, "end": v(154.52, 113.39) * mm});
            skEllipticalArc(sketch, "E369", {});
            skLineSegment(sketch, "E370", {"start": v(146.06, -94) * mm, "end": v(158.25, -91.78) * mm});
            skEllipticalArc(sketch, "E371", {});
            skLineSegment(sketch, "E372", {"start": v(169.07, -110.91) * mm, "end": v(154.52, -113.39) * mm});
            skEllipticalArc(sketch, "E373", {});
            skLineSegment(sketch, "E374", {"start": v(-67.56, 94) * mm, "end": v(-79.75, 91.78) * mm});
            skEllipticalArc(sketch, "E375", {});
            skLineSegment(sketch, "E376", {"start": v(154.52, 113.39) * mm, "end": v(169.07, 110.91) * mm});
            skLineSegment(sketch, "E377", {"start": v(146.21, -94.55) * mm, "end": v(158.4, -92.33) * mm});
            skEllipticalArc(sketch, "E378", {});
            skEllipticalArc(sketch, "E379", {});
            skEllipticalArc(sketch, "E380", {});
            skEllipticalArc(sketch, "E381", {});
            skLineSegment(sketch, "E382", {"start": v(169.04, -110.05) * mm, "end": v(154.47, -112.53) * mm});
            skCircle(sketch, "E383", {"center": v(161.75, -104.5) * mm, "radius": 3.7 * mm});
            skCircle(sketch, "E384", {"center": v(-83.25, -104.5) * mm, "radius": 3.7 * mm});
            skCircle(sketch, "E385", {"center": v(161.75, 104.5) * mm, "radius": 3.7 * mm});
            skCircle(sketch, "E386", {"center": v(-83.25, 104.5) * mm, "radius": 3.7 * mm});
            skLineSegment(sketch, "E387", {"start": v(158.25, 91.78) * mm, "end": v(146.06, 94) * mm});
            skEllipticalArc(sketch, "E388", {});
            skLineSegment(sketch, "E389", {"start": v(-79.75, -91.78) * mm, "end": v(-67.56, -94) * mm});
            skLineSegment(sketch, "E390", {"start": v(-90.57, 110.91) * mm, "end": v(-76.02, 113.39) * mm});
            skEllipticalArc(sketch, "E391", {});
            skLineSegment(sketch, "E392", {"start": v(-64.87, 115.47) * mm, "end": v(-64.88, 115.47) * mm});
            skEllipticalArc(sketch, "E393", {});
            skLineSegment(sketch, "E394", {"start": v(-64.48, 115.5) * mm, "end": v(-64.53, 115.5) * mm});
            skLineSegment(sketch, "E395", {"start": v(-62.35, 114.93) * mm, "end": v(-62.39, 115.06) * mm});
            skLineSegment(sketch, "E396", {"start": v(-62.39, 115.06) * mm, "end": v(-62.43, 115.18) * mm});
            skLineSegment(sketch, "E397", {"start": v(-62.43, 115.18) * mm, "end": v(-62.49, 115.28) * mm});
            skLineSegment(sketch, "E398", {"start": v(-62.49, 115.28) * mm, "end": v(-62.55, 115.37) * mm});
            skLineSegment(sketch, "E399", {"start": v(-62.55, 115.37) * mm, "end": v(-62.62, 115.45) * mm});
            skLineSegment(sketch, "E400", {"start": v(-62.62, 115.45) * mm, "end": v(-62.7, 115.5) * mm});
            skLineSegment(sketch, "E401", {"start": v(-62.7, 115.5) * mm, "end": v(-62.77, 115.54) * mm});
            skLineSegment(sketch, "E402", {"start": v(-62.77, 115.54) * mm, "end": v(-62.85, 115.56) * mm});
            skLineSegment(sketch, "E403", {"start": v(-64.11, 114.85) * mm, "end": v(-64.14, 114.97) * mm});
            skLineSegment(sketch, "E404", {"start": v(-64.14, 114.97) * mm, "end": v(-64.17, 115.09) * mm});
            skLineSegment(sketch, "E405", {"start": v(-64.17, 115.09) * mm, "end": v(-64.21, 115.19) * mm});
            skLineSegment(sketch, "E406", {"start": v(-64.21, 115.19) * mm, "end": v(-64.26, 115.28) * mm});
            skLineSegment(sketch, "E407", {"start": v(-64.26, 115.28) * mm, "end": v(-64.3, 115.36) * mm});
            skLineSegment(sketch, "E408", {"start": v(-64.3, 115.36) * mm, "end": v(-64.36, 115.42) * mm});
            skLineSegment(sketch, "E409", {"start": v(-64.36, 115.42) * mm, "end": v(-64.42, 115.47) * mm});
            skLineSegment(sketch, "E410", {"start": v(-64.42, 115.47) * mm, "end": v(-64.48, 115.5) * mm});
            skLineSegment(sketch, "E411", {"start": v(-62.85, -115.56) * mm, "end": v(-62.77, -115.54) * mm});
            skLineSegment(sketch, "E412", {"start": v(-62.77, -115.54) * mm, "end": v(-62.7, -115.5) * mm});
            skLineSegment(sketch, "E413", {"start": v(-62.7, -115.5) * mm, "end": v(-62.62, -115.45) * mm});
            skLineSegment(sketch, "E414", {"start": v(-62.62, -115.45) * mm, "end": v(-62.55, -115.37) * mm});
            skLineSegment(sketch, "E415", {"start": v(-62.55, -115.37) * mm, "end": v(-62.49, -115.28) * mm});
            skLineSegment(sketch, "E416", {"start": v(-62.49, -115.28) * mm, "end": v(-62.43, -115.18) * mm});
            skLineSegment(sketch, "E417", {"start": v(-62.43, -115.18) * mm, "end": v(-62.39, -115.06) * mm});
            skLineSegment(sketch, "E418", {"start": v(-62.39, -115.06) * mm, "end": v(-62.35, -114.93) * mm});
            skLineSegment(sketch, "E419", {"start": v(-64.53, -115.5) * mm, "end": v(-64.48, -115.5) * mm});
            skLineSegment(sketch, "E420", {"start": v(-64.48, -115.5) * mm, "end": v(-64.42, -115.47) * mm});
            skLineSegment(sketch, "E421", {"start": v(-64.42, -115.47) * mm, "end": v(-64.36, -115.42) * mm});
            skLineSegment(sketch, "E422", {"start": v(-64.36, -115.42) * mm, "end": v(-64.3, -115.36) * mm});
            skLineSegment(sketch, "E423", {"start": v(-64.3, -115.36) * mm, "end": v(-64.26, -115.28) * mm});
            skLineSegment(sketch, "E424", {"start": v(-64.26, -115.28) * mm, "end": v(-64.21, -115.19) * mm});
            skLineSegment(sketch, "E425", {"start": v(-64.21, -115.19) * mm, "end": v(-64.17, -115.09) * mm});
            skLineSegment(sketch, "E426", {"start": v(-64.17, -115.09) * mm, "end": v(-64.14, -114.97) * mm});
            skLineSegment(sketch, "E427", {"start": v(-64.14, -114.97) * mm, "end": v(-64.11, -114.85) * mm});
            skLineSegment(sketch, "E428", {"start": v(-64.88, -115.47) * mm, "end": v(-64.87, -115.47) * mm});
            skLineSegment(sketch, "E429", {"start": v(-75.97, -112.53) * mm, "end": v(-76, -112.66) * mm});
            skLineSegment(sketch, "E430", {"start": v(-76, -112.66) * mm, "end": v(-76, -112.8) * mm});
            skLineSegment(sketch, "E431", {"start": v(-76, -112.8) * mm, "end": v(-76.02, -112.91) * mm});
            skLineSegment(sketch, "E432", {"start": v(-76.02, -112.91) * mm, "end": v(-76.03, -113.02) * mm});
            skLineSegment(sketch, "E433", {"start": v(-76.03, -113.02) * mm, "end": v(-76.04, -113.12) * mm});
            skLineSegment(sketch, "E434", {"start": v(-76.04, -113.12) * mm, "end": v(-76.04, -113.2) * mm});
            skLineSegment(sketch, "E435", {"start": v(-76.04, -113.2) * mm, "end": v(-76.04, -113.28) * mm});
            skLineSegment(sketch, "E436", {"start": v(-76.04, -113.28) * mm, "end": v(-76.04, -113.33) * mm});
            skLineSegment(sketch, "E437", {"start": v(-76.04, -113.33) * mm, "end": v(-76.03, -113.37) * mm});
            skLineSegment(sketch, "E438", {"start": v(-76.03, -113.37) * mm, "end": v(-76.02, -113.39) * mm});
            skEllipticalArc(sketch, "E439", {});
            skLineSegment(sketch, "E440", {"start": v(-76.02, -113.39) * mm, "end": v(-90.57, -110.91) * mm});
            skCircle(sketch, "E441", {"center": v(161.75, 104.5) * mm, "radius": 1.75 * mm});
            skCircle(sketch, "E442", {"center": v(161.75, 104.5) * mm, "radius": 3.25 * mm});
            skCircle(sketch, "E443", {"center": v(161.75, -104.5) * mm, "radius": 1.75 * mm});
            skCircle(sketch, "E444", {"center": v(161.75, -104.5) * mm, "radius": 3.25 * mm});
            skCircle(sketch, "E445", {"center": v(-83.25, -104.5) * mm, "radius": 1.75 * mm});
            skCircle(sketch, "E446", {"center": v(-83.25, -104.5) * mm, "radius": 3.25 * mm});
            skCircle(sketch, "E447", {"center": v(-83.25, 104.5) * mm, "radius": 1.75 * mm});
            skCircle(sketch, "E448", {"center": v(-83.25, 104.5) * mm, "radius": 3.25 * mm});
            skCircle(sketch, "E449", {"center": v(161.75, 104.5) * mm, "radius": 1.25 * mm});
            skCircle(sketch, "E450", {"center": v(161.75, -104.5) * mm, "radius": 1.25 * mm});
            skCircle(sketch, "E451", {"center": v(-83.25, -104.5) * mm, "radius": 1.25 * mm});
            skCircle(sketch, "E452", {"center": v(-83.25, 104.5) * mm, "radius": 1.25 * mm});
            skLineSegment(sketch, "E453", {"start": v(-60.98, 114.72) * mm, "end": v(-58.14, 109.43) * mm});
            skLineSegment(sketch, "E454", {"start": v(-53.07, 100) * mm, "end": v(-51.5, 97.08) * mm});
            skLineSegment(sketch, "E455", {"start": v(-53.6, 101) * mm, "end": v(-53.07, 100) * mm});
            skLineSegment(sketch, "E456", {"start": v(-58.14, 109.43) * mm, "end": v(-53.6, 101) * mm});
            skLineSegment(sketch, "E457", {"start": v(136.64, 109.43) * mm, "end": v(139.48, 114.72) * mm});
            skLineSegment(sketch, "E458", {"start": v(130, 97.08) * mm, "end": v(131.57, 100) * mm});
            skLineSegment(sketch, "E459", {"start": v(131.57, 100) * mm, "end": v(132.1, 101) * mm});
            skLineSegment(sketch, "E460", {"start": v(132.1, 101) * mm, "end": v(136.64, 109.43) * mm});
            skLineSegment(sketch, "E461", {"start": v(139.48, 114.72) * mm, "end": v(140.85, 114.93) * mm});
            skLineSegment(sketch, "E462", {"start": v(-60.98, 114.72) * mm, "end": v(139.48, 114.72) * mm});
            skLineSegment(sketch, "E463", {"start": v(-62.35, 114.94) * mm, "end": v(-60.98, 114.72) * mm});
            skArc(sketch, "E464", {"start": v(-51.78, -97) * mm, "mid": v(-51.76, -96.76) * mm, "end": v(-51.8, -96.52) * mm});
            skLineSegment(sketch, "E465", {"start": v(-51.79, -97.1) * mm, "end": v(-51.78, -97) * mm});
            skLineSegment(sketch, "E466", {"start": v(130, 97.08) * mm, "end": v(130.29, 97.1) * mm});
            skArc(sketch, "E467", {"start": v(130.28, 97) * mm, "mid": v(130.26, 96.76) * mm, "end": v(130.3, 96.52) * mm});
            skLineSegment(sketch, "E468", {"start": v(130.28, 97) * mm, "end": v(130.29, 97.1) * mm});
            skLineSegment(sketch, "E469", {"start": v(130.29, 97.1) * mm, "end": v(131.36, 97) * mm});
            skArc(sketch, "E470", {"start": v(130.3, -96.52) * mm, "mid": v(130.26, -96.76) * mm, "end": v(130.28, -97) * mm});
            skLineSegment(sketch, "E471", {"start": v(130.28, -97) * mm, "end": v(130.29, -97.1) * mm});
            skLineSegment(sketch, "E472", {"start": v(130, 97.08) * mm, "end": v(-51.5, 97.08) * mm});
            skLineSegment(sketch, "E473", {"start": v(-51.79, 97.1) * mm, "end": v(-51.5, 97.08) * mm});
            skArc(sketch, "E474", {"start": v(-51.8, 96.52) * mm, "mid": v(-51.76, 96.76) * mm, "end": v(-51.78, 97) * mm});
            skLineSegment(sketch, "E475", {"start": v(-52.86, 97) * mm, "end": v(-51.79, 97.1) * mm});
            skLineSegment(sketch, "E476", {"start": v(-51.79, 97.1) * mm, "end": v(-51.78, 97) * mm});
            skArc(sketch, "E477", {"start": v(-91.37, -109.07) * mm, "mid": v(-91.14, -109.71) * mm, "end": v(-90.54, -110.05) * mm});
            skArc(sketch, "E478", {"start": v(-90.54, 110.05) * mm, "mid": v(-91.14, 109.71) * mm, "end": v(-91.37, 109.07) * mm});
            skArc(sketch, "E479", {"start": v(-79.9, 92.33) * mm, "mid": v(-80.5, 91.98) * mm, "end": v(-80.73, 91.34) * mm});
            skArc(sketch, "E480", {"start": v(-80.73, -91.34) * mm, "mid": v(-80.5, -91.98) * mm, "end": v(-79.9, -92.33) * mm});
            skLineSegment(sketch, "E481", {"start": v(140.85, -114.93) * mm, "end": v(141.4, -114.9) * mm});
            skLineSegment(sketch, "E482", {"start": v(131.36, -97.01) * mm, "end": v(131.44, -97) * mm});
            skLineSegment(sketch, "E483", {"start": v(131.44, -97) * mm, "end": v(135.17, -96.46) * mm});
            skLineSegment(sketch, "E484", {"start": v(135.17, -96.45) * mm, "end": v(137.99, -96) * mm});
            skLineSegment(sketch, "E485", {"start": v(137.99, -96.01) * mm, "end": v(146.21, -94.56) * mm});
            skArc(sketch, "E486", {"start": v(142.61, -114.85) * mm, "mid": v(142.7, -114.84) * mm, "end": v(142.8, -114.83) * mm});
            skLineSegment(sketch, "E487", {"start": v(141.4, -114.9) * mm, "end": v(142.61, -114.85) * mm});
            skLineSegment(sketch, "E488", {"start": v(142.8, -114.83) * mm, "end": v(143.57, -114.67) * mm});
            skLineSegment(sketch, "E489", {"start": v(143.57, -114.65) * mm, "end": v(154.47, -112.52) * mm});
            skLineSegment(sketch, "E490", {"start": v(139.49, 112.35) * mm, "end": v(140.85, 114.93) * mm});
            skLineSegment(sketch, "E491", {"start": v(140.85, 114.93) * mm, "end": v(141.4, 114.9) * mm});
            skLineSegment(sketch, "E492", {"start": v(141.4, 114.9) * mm, "end": v(142.61, 114.85) * mm});
            skArc(sketch, "E493", {"start": v(142.8, 114.83) * mm, "mid": v(142.7, 114.84) * mm, "end": v(142.61, 114.85) * mm});
            skLineSegment(sketch, "E494", {"start": v(142.8, 114.83) * mm, "end": v(143.57, 114.67) * mm});
            skLineSegment(sketch, "E495", {"start": v(143.57, 114.65) * mm, "end": v(154.47, 112.52) * mm});
            skLineSegment(sketch, "E496", {"start": v(137.99, 96.01) * mm, "end": v(146.21, 94.56) * mm});
            skLineSegment(sketch, "E497", {"start": v(135.17, 96.45) * mm, "end": v(137.99, 96) * mm});
            skLineSegment(sketch, "E498", {"start": v(131.44, 97) * mm, "end": v(135.17, 96.46) * mm});
            skLineSegment(sketch, "E499", {"start": v(131.36, 97.01) * mm, "end": v(131.44, 97) * mm});
            skLineSegment(sketch, "E500", {"start": v(131.36, 97.01) * mm, "end": v(132.95, 100) * mm});
            skLineSegment(sketch, "E501", {"start": v(132.95, 100) * mm, "end": v(133.48, 101) * mm});
            skLineSegment(sketch, "E502", {"start": v(133.48, 101) * mm, "end": v(139.49, 112.35) * mm});
            skArc(sketch, "E503", {"start": v(-79.75, 91.78) * mm, "mid": v(-80.04, 91.61) * mm, "end": v(-80.17, 91.3) * mm});
            skLineSegment(sketch, "E504", {"start": v(136.12, -95.7) * mm, "end": v(146.07, -94.02) * mm});
            skLineSegment(sketch, "E505", {"start": v(133.93, -96) * mm, "end": v(136.12, -95.68) * mm});
            skLineSegment(sketch, "E506", {"start": v(131.55, -96.33) * mm, "end": v(133.93, -96) * mm});
            skLineSegment(sketch, "E507", {"start": v(130.3, -96.52) * mm, "end": v(131.55, -96.33) * mm});
            skLineSegment(sketch, "E508", {"start": v(130.3, -96.52) * mm, "end": v(130.3, -96.52) * mm});
            skFitSpline(sketch, "E509", {"points": [v(130.3, -96.52) * mm, v(130.3, -96.52) * mm, v(130.3, -96.52) * mm, v(130.3, -96.52) * mm]});
            skLineSegment(sketch, "E510", {"start": v(171.25, 109.39) * mm, "end": v(171.23, 109.67) * mm});
            skLineSegment(sketch, "E511", {"start": v(171.23, 109.67) * mm, "end": v(171.17, 109.94) * mm});
            skLineSegment(sketch, "E512", {"start": v(171.17, 109.94) * mm, "end": v(171.08, 110.2) * mm});
            skLineSegment(sketch, "E513", {"start": v(171.08, 110.2) * mm, "end": v(170.95, 110.45) * mm});
            skLineSegment(sketch, "E514", {"start": v(170.95, 110.45) * mm, "end": v(170.78, 110.67) * mm});
            skLineSegment(sketch, "E515", {"start": v(170.78, 110.67) * mm, "end": v(170.59, 110.87) * mm});
            skLineSegment(sketch, "E516", {"start": v(170.59, 110.87) * mm, "end": v(170.37, 111.04) * mm});
            skLineSegment(sketch, "E517", {"start": v(170.37, 111.04) * mm, "end": v(170.13, 111.18) * mm});
            skLineSegment(sketch, "E518", {"start": v(170.13, 111.18) * mm, "end": v(169.87, 111.29) * mm});
            skLineSegment(sketch, "E519", {"start": v(169.87, 111.29) * mm, "end": v(169.6, 111.35) * mm});
            skArc(sketch, "E520", {"start": v(170.72, 108.95) * mm, "mid": v(170.26, 110.23) * mm, "end": v(169.07, 110.91) * mm});
            skLineSegment(sketch, "E521", {"start": v(171.25, -109.39) * mm, "end": v(171.25, 109.39) * mm});
            skLineSegment(sketch, "E522", {"start": v(170.72, 108.95) * mm, "end": v(171.25, 109.39) * mm});
            skEllipticalArc(sketch, "E523", {});
            skArc(sketch, "E524", {"start": v(169.07, -110.91) * mm, "mid": v(170.26, -110.23) * mm, "end": v(170.72, -108.95) * mm});
            skLineSegment(sketch, "E525", {"start": v(171.25, -109.39) * mm, "end": v(170.72, -108.95) * mm});
            skLineSegment(sketch, "E526", {"start": v(143.4, -115.47) * mm, "end": v(145.32, -115.08) * mm});
            skLineSegment(sketch, "E527", {"start": v(145.31, -115.06) * mm, "end": v(154.52, -113.38) * mm});
            skLineSegment(sketch, "E528", {"start": v(169.07, -110.91) * mm, "end": v(169.6, -111.35) * mm});
            skLineSegment(sketch, "E529", {"start": v(143.42, -115.97) * mm, "end": v(169.6, -111.35) * mm});
            skLineSegment(sketch, "E530", {"start": v(143.38, -115.47) * mm, "end": v(143.4, -115.47) * mm});
            skArc(sketch, "E531", {"start": v(143.03, -115.5) * mm, "mid": v(143.2, -115.5) * mm, "end": v(143.38, -115.47) * mm});
            skLineSegment(sketch, "E532", {"start": v(143.42, -115.97) * mm, "end": v(143.38, -115.47) * mm});
            skLineSegment(sketch, "E533", {"start": v(143.08, -116) * mm, "end": v(143.42, -115.97) * mm});
            skLineSegment(sketch, "E534", {"start": v(-62.85, -115.56) * mm, "end": v(-60.98, -115.59) * mm});
            skLineSegment(sketch, "E535", {"start": v(-60.98, -115.59) * mm, "end": v(139.48, -115.59) * mm});
            skLineSegment(sketch, "E536", {"start": v(139.48, -115.6) * mm, "end": v(141.35, -115.56) * mm});
            skLineSegment(sketch, "E537", {"start": v(141.35, -115.56) * mm, "end": v(143.03, -115.5) * mm});
            skLineSegment(sketch, "E538", {"start": v(143.03, -115.5) * mm, "end": v(143.08, -116) * mm});
            skLineSegment(sketch, "E539", {"start": v(137.72, -116) * mm, "end": v(143.08, -116) * mm});
            skEllipticalArc(sketch, "E540", {});
            skLineSegment(sketch, "E541", {"start": v(122.23, -116.42) * mm, "end": v(-43.73, -116.42) * mm});
            skEllipticalArc(sketch, "E542", {});
            skLineSegment(sketch, "E543", {"start": v(-64.58, -116) * mm, "end": v(-59.22, -116) * mm});
            skLineSegment(sketch, "E544", {"start": v(-64.58, -116) * mm, "end": v(-64.53, -115.5) * mm});
            skLineSegment(sketch, "E545", {"start": v(-64.92, -115.97) * mm, "end": v(-64.58, -116) * mm});
            skArc(sketch, "E546", {"start": v(158.25, -91.78) * mm, "mid": v(158.54, -91.61) * mm, "end": v(158.67, -91.3) * mm});
            skLineSegment(sketch, "E547", {"start": v(157.61, -91.65) * mm, "end": v(158.25, -91.78) * mm});
            skLineSegment(sketch, "E548", {"start": v(158.67, -91.3) * mm, "end": v(158.03, -91.16) * mm});
            skLineSegment(sketch, "E549", {"start": v(-51.8, 96.52) * mm, "end": v(-51.5, 96.52) * mm});
            skLineSegment(sketch, "E550", {"start": v(-51.5, 96.52) * mm, "end": v(130, 96.52) * mm});
            skLineSegment(sketch, "E551", {"start": v(130, 96.52) * mm, "end": v(130.3, 96.52) * mm});
            skLineSegment(sketch, "E552", {"start": v(-79.11, 91.65) * mm, "end": v(-79.75, 91.78) * mm});
            skLineSegment(sketch, "E553", {"start": v(-67.57, 94.02) * mm, "end": v(-57.62, 95.69) * mm});
            skLineSegment(sketch, "E554", {"start": v(-57.62, 95.68) * mm, "end": v(-55.43, 96) * mm});
            skLineSegment(sketch, "E555", {"start": v(-55.43, 96) * mm, "end": v(-53.05, 96.33) * mm});
            skLineSegment(sketch, "E556", {"start": v(-53.05, 96.33) * mm, "end": v(-51.8, 96.52) * mm});
            skLineSegment(sketch, "E557", {"start": v(-51.8, 96.52) * mm, "end": v(-51.8, 96.52) * mm});
            skFitSpline(sketch, "E558", {"points": [v(-51.8, 96.52) * mm, v(-51.8, 96.52) * mm, v(-51.8, 96.52) * mm, v(-51.8, 96.52) * mm]});
            skLineSegment(sketch, "E559", {"start": v(-51.8, 96.52) * mm, "end": v(-51.8, 96.47) * mm});
            skEllipticalArc(sketch, "E560", {});
            skArc(sketch, "E561", {"start": v(-92.22, -108.95) * mm, "mid": v(-91.76, -110.23) * mm, "end": v(-90.57, -110.91) * mm});
            skLineSegment(sketch, "E562", {"start": v(-92.75, 109.39) * mm, "end": v(-92.75, -109.39) * mm});
            skLineSegment(sketch, "E563", {"start": v(-92.22, -108.95) * mm, "end": v(-92.75, -109.39) * mm});
            skLineSegment(sketch, "E564", {"start": v(-91.1, 111.35) * mm, "end": v(-91.37, 111.29) * mm});
            skLineSegment(sketch, "E565", {"start": v(-91.37, 111.29) * mm, "end": v(-91.63, 111.18) * mm});
            skLineSegment(sketch, "E566", {"start": v(-91.63, 111.18) * mm, "end": v(-91.87, 111.04) * mm});
            skLineSegment(sketch, "E567", {"start": v(-91.87, 111.04) * mm, "end": v(-92.09, 110.87) * mm});
            skLineSegment(sketch, "E568", {"start": v(-92.09, 110.87) * mm, "end": v(-92.28, 110.67) * mm});
            skLineSegment(sketch, "E569", {"start": v(-92.28, 110.67) * mm, "end": v(-92.45, 110.45) * mm});
            skLineSegment(sketch, "E570", {"start": v(-92.45, 110.45) * mm, "end": v(-92.58, 110.2) * mm});
            skLineSegment(sketch, "E571", {"start": v(-92.58, 110.2) * mm, "end": v(-92.67, 109.94) * mm});
            skLineSegment(sketch, "E572", {"start": v(-92.67, 109.94) * mm, "end": v(-92.73, 109.67) * mm});
            skLineSegment(sketch, "E573", {"start": v(-92.73, 109.67) * mm, "end": v(-92.75, 109.39) * mm});
            skArc(sketch, "E574", {"start": v(-90.57, 110.91) * mm, "mid": v(-91.76, 110.23) * mm, "end": v(-92.22, 108.95) * mm});
            skLineSegment(sketch, "E575", {"start": v(-92.75, 109.39) * mm, "end": v(-92.22, 108.95) * mm});
            skLineSegment(sketch, "E576", {"start": v(169.6, 111.35) * mm, "end": v(143.42, 115.97) * mm});
            skLineSegment(sketch, "E577", {"start": v(169.6, 111.35) * mm, "end": v(169.07, 110.91) * mm});
            skLineSegment(sketch, "E578", {"start": v(145.31, 115.06) * mm, "end": v(154.52, 113.38) * mm});
            skLineSegment(sketch, "E579", {"start": v(143.4, 115.47) * mm, "end": v(145.32, 115.08) * mm});
            skLineSegment(sketch, "E580", {"start": v(143.38, 115.47) * mm, "end": v(143.4, 115.47) * mm});
            skLineSegment(sketch, "E581", {"start": v(147.36, -97) * mm, "end": v(147.55, -97.42) * mm});
            skLineSegment(sketch, "E582", {"start": v(146.89, -96) * mm, "end": v(147.36, -97) * mm});
            skLineSegment(sketch, "E583", {"start": v(146.21, -94.55) * mm, "end": v(146.89, -96) * mm});
            skArc(sketch, "E584", {"start": v(158.4, -92.33) * mm, "mid": v(159, -91.98) * mm, "end": v(159.23, -91.34) * mm});
            skArc(sketch, "E585", {"start": v(159.23, 91.34) * mm, "mid": v(159, 91.98) * mm, "end": v(158.4, 92.33) * mm});
            skLineSegment(sketch, "E586", {"start": v(146.21, 94.55) * mm, "end": v(146.89, 96) * mm});
            skLineSegment(sketch, "E587", {"start": v(146.89, 96) * mm, "end": v(147.36, 97) * mm});
            skLineSegment(sketch, "E588", {"start": v(147.36, 97) * mm, "end": v(147.55, 97.42) * mm});
            skLineSegment(sketch, "E589", {"start": v(147.55, 97.42) * mm, "end": v(148.75, 100) * mm});
            skLineSegment(sketch, "E590", {"start": v(148.75, 100) * mm, "end": v(149.21, 101) * mm});
            skLineSegment(sketch, "E591", {"start": v(149.22, 101) * mm, "end": v(154.48, 112.53) * mm});
            skArc(sketch, "E592", {"start": v(169.87, 109.07) * mm, "mid": v(169.64, 109.71) * mm, "end": v(169.04, 110.05) * mm});
            skArc(sketch, "E593", {"start": v(169.04, -110.05) * mm, "mid": v(169.64, -109.71) * mm, "end": v(169.87, -109.07) * mm});
            skLineSegment(sketch, "E594", {"start": v(149.22, -101) * mm, "end": v(154.48, -112.53) * mm});
            skLineSegment(sketch, "E595", {"start": v(148.75, -100) * mm, "end": v(149.21, -101) * mm});
            skLineSegment(sketch, "E596", {"start": v(147.55, -97.42) * mm, "end": v(148.75, -100) * mm});
            skLineSegment(sketch, "E597", {"start": v(130.3, 96.52) * mm, "end": v(130.3, 96.47) * mm});
            skFitSpline(sketch, "E598", {"points": [v(130.3, 96.52) * mm, v(130.3, 96.52) * mm, v(130.3, 96.52) * mm, v(130.3, 96.52) * mm]});
            skLineSegment(sketch, "E599", {"start": v(130.3, 96.52) * mm, "end": v(130.3, 96.52) * mm});
            skLineSegment(sketch, "E600", {"start": v(130.3, 96.52) * mm, "end": v(131.55, 96.33) * mm});
            skLineSegment(sketch, "E601", {"start": v(131.55, 96.33) * mm, "end": v(133.93, 96) * mm});
            skLineSegment(sketch, "E602", {"start": v(133.93, 96) * mm, "end": v(136.12, 95.68) * mm});
            skLineSegment(sketch, "E603", {"start": v(136.12, 95.7) * mm, "end": v(146.07, 94.02) * mm});
            skLineSegment(sketch, "E604", {"start": v(-80.17, 91.3) * mm, "end": v(-79.53, 91.16) * mm});
            skLineSegment(sketch, "E605", {"start": v(158.25, 91.78) * mm, "end": v(157.61, 91.65) * mm});
            skArc(sketch, "E606", {"start": v(158.67, 91.3) * mm, "mid": v(158.54, 91.61) * mm, "end": v(158.25, 91.78) * mm});
            skLineSegment(sketch, "E607", {"start": v(158.03, 91.16) * mm, "end": v(158.67, 91.3) * mm});
            skArc(sketch, "E608", {"start": v(-80.17, -91.3) * mm, "mid": v(-80.04, -91.61) * mm, "end": v(-79.75, -91.78) * mm});
            skLineSegment(sketch, "E609", {"start": v(-79.53, -91.16) * mm, "end": v(-80.17, -91.3) * mm});
            skFitSpline(sketch, "E610", {"points": [v(-51.8, -96.52) * mm, v(-51.8, -96.52) * mm, v(-51.8, -96.52) * mm, v(-51.8, -96.52) * mm]});
            skLineSegment(sketch, "E611", {"start": v(-51.8, -96.52) * mm, "end": v(-51.8, -96.52) * mm});
            skLineSegment(sketch, "E612", {"start": v(-53.05, -96.33) * mm, "end": v(-51.8, -96.52) * mm});
            skLineSegment(sketch, "E613", {"start": v(-55.43, -96) * mm, "end": v(-53.05, -96.33) * mm});
            skLineSegment(sketch, "E614", {"start": v(-57.62, -95.68) * mm, "end": v(-55.43, -96) * mm});
            skLineSegment(sketch, "E615", {"start": v(-67.57, -94.02) * mm, "end": v(-57.62, -95.69) * mm});
            skLineSegment(sketch, "E616", {"start": v(-79.75, -91.78) * mm, "end": v(-79.11, -91.65) * mm});
            skLineSegment(sketch, "E617", {"start": v(130.3, -96.52) * mm, "end": v(130.3, -96.47) * mm});
            skLineSegment(sketch, "E618", {"start": v(130, -96.52) * mm, "end": v(130.3, -96.52) * mm});
            skLineSegment(sketch, "E619", {"start": v(130, -96.52) * mm, "end": v(-51.5, -96.52) * mm});
            skLineSegment(sketch, "E620", {"start": v(-51.8, -96.52) * mm, "end": v(-51.5, -96.52) * mm});
            skLineSegment(sketch, "E621", {"start": v(-51.8, -96.52) * mm, "end": v(-51.8, -96.47) * mm});
            skArc(sketch, "E622", {"start": v(143.38, 115.47) * mm, "mid": v(143.2, 115.5) * mm, "end": v(143.03, 115.5) * mm});
            skLineSegment(sketch, "E623", {"start": v(143.42, 115.97) * mm, "end": v(143.08, 116) * mm});
            skLineSegment(sketch, "E624", {"start": v(143.38, 115.47) * mm, "end": v(143.42, 115.97) * mm});
            skLineSegment(sketch, "E625", {"start": v(141.35, 115.56) * mm, "end": v(143.03, 115.5) * mm});
            skLineSegment(sketch, "E626", {"start": v(139.48, 115.6) * mm, "end": v(141.35, 115.56) * mm});
            skLineSegment(sketch, "E627", {"start": v(139.48, 115.59) * mm, "end": v(-60.98, 115.59) * mm});
            skLineSegment(sketch, "E628", {"start": v(-62.85, 115.56) * mm, "end": v(-60.98, 115.59) * mm});
            skLineSegment(sketch, "E629", {"start": v(-59.22, 116) * mm, "end": v(-64.58, 116) * mm});
            skEllipticalArc(sketch, "E630", {});
            skLineSegment(sketch, "E631", {"start": v(-43.73, 116.42) * mm, "end": v(121.84, 116.42) * mm});
            skEllipticalArc(sketch, "E632", {});
            skLineSegment(sketch, "E633", {"start": v(143.08, 116) * mm, "end": v(137.72, 116) * mm});
            skLineSegment(sketch, "E634", {"start": v(143.08, 116) * mm, "end": v(143.03, 115.5) * mm});
            skLineSegment(sketch, "E635", {"start": v(-64.58, 116) * mm, "end": v(-64.92, 115.97) * mm});
            skLineSegment(sketch, "E636", {"start": v(-64.53, 115.5) * mm, "end": v(-64.58, 116) * mm});
            skLineSegment(sketch, "E637", {"start": v(-90.57, 110.91) * mm, "end": v(-91.1, 111.35) * mm});
            skLineSegment(sketch, "E638", {"start": v(-64.92, 115.97) * mm, "end": v(-91.1, 111.35) * mm});
            skLineSegment(sketch, "E639", {"start": v(-64.92, 115.97) * mm, "end": v(-64.88, 115.47) * mm});
            skLineSegment(sketch, "E640", {"start": v(-64.9, 115.47) * mm, "end": v(-64.88, 115.47) * mm});
            skLineSegment(sketch, "E641", {"start": v(-76.02, 113.37) * mm, "end": v(-66.82, 115.07) * mm});
            skLineSegment(sketch, "E642", {"start": v(-66.82, 115.08) * mm, "end": v(-64.9, 115.47) * mm});
            skArc(sketch, "E643", {"start": v(-64.53, 115.5) * mm, "mid": v(-64.7, 115.5) * mm, "end": v(-64.88, 115.47) * mm});
            skLineSegment(sketch, "E644", {"start": v(-64.53, 115.5) * mm, "end": v(-62.85, 115.56) * mm});
            skLineSegment(sketch, "E645", {"start": v(-62.9, 114.9) * mm, "end": v(-62.35, 114.93) * mm});
            skLineSegment(sketch, "E646", {"start": v(-62.35, 114.93) * mm, "end": v(-60.99, 112.35) * mm});
            skLineSegment(sketch, "E647", {"start": v(-60.99, 112.35) * mm, "end": v(-54.98, 101) * mm});
            skLineSegment(sketch, "E648", {"start": v(-54.98, 101) * mm, "end": v(-54.45, 100) * mm});
            skLineSegment(sketch, "E649", {"start": v(-54.45, 100) * mm, "end": v(-52.86, 97.01) * mm});
            skLineSegment(sketch, "E650", {"start": v(-52.94, 97) * mm, "end": v(-52.86, 97.01) * mm});
            skLineSegment(sketch, "E651", {"start": v(-56.67, 96.46) * mm, "end": v(-52.94, 97) * mm});
            skLineSegment(sketch, "E652", {"start": v(-59.49, 96) * mm, "end": v(-56.67, 96.45) * mm});
            skLineSegment(sketch, "E653", {"start": v(-67.71, 94.56) * mm, "end": v(-59.49, 96.01) * mm});
            skLineSegment(sketch, "E654", {"start": v(-68.39, 96) * mm, "end": v(-67.71, 94.55) * mm});
            skLineSegment(sketch, "E655", {"start": v(-68.86, 97) * mm, "end": v(-68.39, 96) * mm});
            skLineSegment(sketch, "E656", {"start": v(39.25, -118.42) * mm, "end": v(39.25, 118.42) * mm});
            skLineSegment(sketch, "E657", {"start": v(173.25, 0) * mm, "end": v(-94.75, 0) * mm});
            skLineSegment(sketch, "E658", {"start": v(-83.25, 110.2) * mm, "end": v(-83.25, 98.8) * mm});
            skLineSegment(sketch, "E659", {"start": v(-88.95, 104.5) * mm, "end": v(-77.55, 104.5) * mm});
            skLineSegment(sketch, "E660", {"start": v(161.75, 110.2) * mm, "end": v(161.75, 98.8) * mm});
            skLineSegment(sketch, "E661", {"start": v(156.05, 104.5) * mm, "end": v(167.45, 104.5) * mm});
            skLineSegment(sketch, "E662", {"start": v(161.75, -98.8) * mm, "end": v(161.75, -110.2) * mm});
            skLineSegment(sketch, "E663", {"start": v(156.05, -104.5) * mm, "end": v(167.45, -104.5) * mm});
            skLineSegment(sketch, "E664", {"start": v(-83.25, -98.8) * mm, "end": v(-83.25, -110.2) * mm});
            skLineSegment(sketch, "E665", {"start": v(-88.95, -104.5) * mm, "end": v(-77.55, -104.5) * mm});
            skLineSegment(sketch, "E666", {"start": v(-73.25, 92.5) * mm, "end": v(-73.25, 82.5) * mm});
            skCircle(sketch, "E667", {"center": v(-73.25, 87.5) * mm, "radius": 3 * mm});
            skCircle(sketch, "E668", {"center": v(-73.25, 87.5) * mm, "radius": 1.5 * mm});
            skCircle(sketch, "E669", {"center": v(-73.25, 87.5) * mm, "radius": 1.2 * mm});
            skLineSegment(sketch, "E670", {"start": v(-78.25, 87.5) * mm, "end": v(-68.25, 87.5) * mm});
            skLineSegment(sketch, "E671", {"start": v(34.25, 87.5) * mm, "end": v(44.25, 87.5) * mm});
            skCircle(sketch, "E672", {"center": v(39.25, 87.5) * mm, "radius": 3 * mm});
            skCircle(sketch, "E673", {"center": v(39.25, 87.5) * mm, "radius": 1.5 * mm});
            skCircle(sketch, "E674", {"center": v(39.25, 87.5) * mm, "radius": 1.2 * mm});
            skCircle(sketch, "E675", {"center": v(151.75, 87.5) * mm, "radius": 3 * mm});
            skCircle(sketch, "E676", {"center": v(151.75, 87.5) * mm, "radius": 1.5 * mm});
            skCircle(sketch, "E677", {"center": v(151.75, 87.5) * mm, "radius": 1.2 * mm});
            skLineSegment(sketch, "E678", {"start": v(151.75, 92.5) * mm, "end": v(151.75, 82.5) * mm});
            skLineSegment(sketch, "E679", {"start": v(146.75, 87.5) * mm, "end": v(156.75, 87.5) * mm});
            skCircle(sketch, "E680", {"center": v(151.75, 0) * mm, "radius": 3 * mm});
            skCircle(sketch, "E681", {"center": v(151.75, 0) * mm, "radius": 1.5 * mm});
            skCircle(sketch, "E682", {"center": v(151.75, 0) * mm, "radius": 1.2 * mm});
            skLineSegment(sketch, "E683", {"start": v(151.75, 5) * mm, "end": v(151.75, -5) * mm});
            skCircle(sketch, "E684", {"center": v(151.75, -87.5) * mm, "radius": 3 * mm});
            skCircle(sketch, "E685", {"center": v(151.75, -87.5) * mm, "radius": 1.2 * mm});
            skCircle(sketch, "E686", {"center": v(151.75, -87.5) * mm, "radius": 1.5 * mm});
            skLineSegment(sketch, "E687", {"start": v(151.75, -82.5) * mm, "end": v(151.75, -92.5) * mm});
            skLineSegment(sketch, "E688", {"start": v(146.75, -87.5) * mm, "end": v(156.75, -87.5) * mm});
            skCircle(sketch, "E689", {"center": v(39.25, -87.5) * mm, "radius": 3 * mm});
            skCircle(sketch, "E690", {"center": v(39.25, -87.5) * mm, "radius": 1.5 * mm});
            skCircle(sketch, "E691", {"center": v(39.25, -87.5) * mm, "radius": 1.2 * mm});
            skLineSegment(sketch, "E692", {"start": v(34.25, -87.5) * mm, "end": v(44.25, -87.5) * mm});
            skCircle(sketch, "E693", {"center": v(-73.25, -87.5) * mm, "radius": 3 * mm});
            skCircle(sketch, "E694", {"center": v(-73.25, -87.5) * mm, "radius": 1.5 * mm});
            skCircle(sketch, "E695", {"center": v(-73.25, -87.5) * mm, "radius": 1.2 * mm});
            skLineSegment(sketch, "E696", {"start": v(-73.25, -82.5) * mm, "end": v(-73.25, -92.5) * mm});
            skLineSegment(sketch, "E697", {"start": v(-78.25, -87.5) * mm, "end": v(-68.25, -87.5) * mm});
            skCircle(sketch, "E698", {"center": v(-73.25, 0) * mm, "radius": 3 * mm});
            skCircle(sketch, "E699", {"center": v(-73.25, 0) * mm, "radius": 1.5 * mm});
            skCircle(sketch, "E700", {"center": v(-73.25, 0) * mm, "radius": 1.2 * mm});
            skLineSegment(sketch, "E701", {"start": v(-73.25, 5) * mm, "end": v(-73.25, -5) * mm});
            skArc(sketch, "E702", {"start": v(-58.25, -67.5) * mm, "mid": v(-40.75, -50) * mm, "end": v(-23.25, -67.5) * mm});
            skArc(sketch, "E703", {"start": v(-23.25, -67.5) * mm, "mid": v(-40.75, -85) * mm, "end": v(-58.25, -67.5) * mm});
            skArc(sketch, "E704", {"start": v(16.75, -63.63) * mm, "mid": v(13.81, -60.6) * mm, "end": v(9.75, -59.5) * mm});
            skLineSegment(sketch, "E705", {"start": v(9.75, -59.5) * mm, "end": v(9.75, -59.5) * mm});
            skArc(sketch, "E706", {"start": v(9.75, -59.5) * mm, "mid": v(5.69, -60.6) * mm, "end": v(2.75, -63.63) * mm});
            skLineSegment(sketch, "E707", {"start": v(2.75, -63.63) * mm, "end": v(2.75, -71.37) * mm});
            skArc(sketch, "E708", {"start": v(2.75, -71.37) * mm, "mid": v(5.69, -74.4) * mm, "end": v(9.75, -75.5) * mm});
            skArc(sketch, "E709", {"start": v(9.75, -75.5) * mm, "mid": v(13.81, -74.4) * mm, "end": v(16.75, -71.37) * mm});
            skLineSegment(sketch, "E710", {"start": v(16.75, -71.37) * mm, "end": v(16.75, -63.63) * mm});
            skArc(sketch, "E711", {"start": v(96.75, -63.63) * mm, "mid": v(93.81, -60.6) * mm, "end": v(89.75, -59.5) * mm});
            skLineSegment(sketch, "E712", {"start": v(89.75, -59.5) * mm, "end": v(89.75, -59.5) * mm});
            skArc(sketch, "E713", {"start": v(89.75, -59.5) * mm, "mid": v(85.69, -60.6) * mm, "end": v(82.75, -63.63) * mm});
            skLineSegment(sketch, "E714", {"start": v(82.75, -63.63) * mm, "end": v(82.75, -71.37) * mm});
            skArc(sketch, "E715", {"start": v(82.75, -71.37) * mm, "mid": v(85.69, -74.4) * mm, "end": v(89.75, -75.5) * mm});
            skArc(sketch, "E716", {"start": v(89.75, -75.5) * mm, "mid": v(93.81, -74.4) * mm, "end": v(96.75, -71.37) * mm});
            skLineSegment(sketch, "E717", {"start": v(96.75, -71.37) * mm, "end": v(96.75, -63.63) * mm});
            skArc(sketch, "E718", {"start": v(56.75, -63.63) * mm, "mid": v(53.81, -60.6) * mm, "end": v(49.75, -59.5) * mm});
            skLineSegment(sketch, "E719", {"start": v(49.75, -59.5) * mm, "end": v(49.75, -59.5) * mm});
            skArc(sketch, "E720", {"start": v(49.75, -59.5) * mm, "mid": v(45.69, -60.6) * mm, "end": v(42.75, -63.63) * mm});
            skLineSegment(sketch, "E721", {"start": v(42.75, -63.63) * mm, "end": v(42.75, -71.37) * mm});
            skArc(sketch, "E722", {"start": v(42.75, -71.37) * mm, "mid": v(45.69, -74.4) * mm, "end": v(49.75, -75.5) * mm});
            skArc(sketch, "E723", {"start": v(49.75, -75.5) * mm, "mid": v(53.81, -74.4) * mm, "end": v(56.75, -71.37) * mm});
            skLineSegment(sketch, "E724", {"start": v(56.75, -71.37) * mm, "end": v(56.75, -63.63) * mm});
            skArc(sketch, "E725", {"start": v(136.75, -63.63) * mm, "mid": v(133.81, -60.6) * mm, "end": v(129.75, -59.5) * mm});
            skLineSegment(sketch, "E726", {"start": v(129.75, -59.5) * mm, "end": v(129.75, -59.5) * mm});
            skArc(sketch, "E727", {"start": v(129.75, -59.5) * mm, "mid": v(125.69, -60.6) * mm, "end": v(122.75, -63.63) * mm});
            skLineSegment(sketch, "E728", {"start": v(122.75, -63.63) * mm, "end": v(122.75, -71.37) * mm});
            skArc(sketch, "E729", {"start": v(122.75, -71.37) * mm, "mid": v(125.69, -74.4) * mm, "end": v(129.75, -75.5) * mm});
            skArc(sketch, "E730", {"start": v(129.75, -75.5) * mm, "mid": v(133.81, -74.4) * mm, "end": v(136.75, -71.37) * mm});
            skLineSegment(sketch, "E731", {"start": v(136.75, -71.37) * mm, "end": v(136.75, -63.63) * mm});
            skArc(sketch, "E732", {"start": v(-17.25, -44.5) * mm, "mid": v(-15.75, -43) * mm, "end": v(-14.25, -44.5) * mm});
            skArc(sketch, "E733", {"start": v(-14.25, -44.5) * mm, "mid": v(-15.75, -46) * mm, "end": v(-17.25, -44.5) * mm});
            skArc(sketch, "E734", {"start": v(-17.25, -34.5) * mm, "mid": v(-15.75, -33) * mm, "end": v(-14.25, -34.5) * mm});
            skArc(sketch, "E735", {"start": v(-14.25, -34.5) * mm, "mid": v(-15.75, -36) * mm, "end": v(-17.25, -34.5) * mm});
            skLineSegment(sketch, "E736", {"start": v(-28.63, -46.5) * mm, "end": v(-52.87, -46.5) * mm});
            skLineSegment(sketch, "E737", {"start": v(-52.87, -46.5) * mm, "end": v(-65, -67.5) * mm});
            skLineSegment(sketch, "E738", {"start": v(-65, -67.5) * mm, "end": v(-52.87, -88.5) * mm});
            skLineSegment(sketch, "E739", {"start": v(-52.87, -88.5) * mm, "end": v(-28.63, -88.5) * mm});
            skLineSegment(sketch, "E740", {"start": v(-28.63, -88.5) * mm, "end": v(-16.5, -67.5) * mm});
            skLineSegment(sketch, "E741", {"start": v(-16.5, -67.5) * mm, "end": v(-28.63, -46.5) * mm});
            skArc(sketch, "E742", {"start": v(-1, -67.5) * mm, "mid": v(9.75, -56.75) * mm, "end": v(20.5, -67.5) * mm});
            skArc(sketch, "E743", {"start": v(20.5, -67.5) * mm, "mid": v(9.75, -78.25) * mm, "end": v(-1, -67.5) * mm});
            skArc(sketch, "E744", {"start": v(39, -67.5) * mm, "mid": v(49.75, -56.75) * mm, "end": v(60.5, -67.5) * mm});
            skArc(sketch, "E745", {"start": v(60.5, -67.5) * mm, "mid": v(49.75, -78.25) * mm, "end": v(39, -67.5) * mm});
            skArc(sketch, "E746", {"start": v(79, -67.5) * mm, "mid": v(89.75, -56.75) * mm, "end": v(100.5, -67.5) * mm});
            skArc(sketch, "E747", {"start": v(100.5, -67.5) * mm, "mid": v(89.75, -78.25) * mm, "end": v(79, -67.5) * mm});
            skArc(sketch, "E748", {"start": v(119, -67.5) * mm, "mid": v(129.75, -56.75) * mm, "end": v(140.5, -67.5) * mm});
            skArc(sketch, "E749", {"start": v(140.5, -67.5) * mm, "mid": v(129.75, -78.25) * mm, "end": v(119, -67.5) * mm});
            skArc(sketch, "E750", {"start": v(-159.25, 16.6) * mm, "mid": v(-162.19, 19.62) * mm, "end": v(-166.25, 20.73) * mm});
            skLineSegment(sketch, "E751", {"start": v(-166.25, 20.73) * mm, "end": v(-166.25, 20.73) * mm});
            skArc(sketch, "E752", {"start": v(-166.25, 20.73) * mm, "mid": v(-170.31, 19.62) * mm, "end": v(-173.25, 16.6) * mm});
            skLineSegment(sketch, "E753", {"start": v(-173.25, 16.6) * mm, "end": v(-173.25, 8.85) * mm});
            skArc(sketch, "E754", {"start": v(-173.25, 8.85) * mm, "mid": v(-170.31, 5.84) * mm, "end": v(-166.25, 4.73) * mm});
            skArc(sketch, "E755", {"start": v(-166.25, 4.73) * mm, "mid": v(-162.19, 5.84) * mm, "end": v(-159.25, 8.85) * mm});
            skLineSegment(sketch, "E756", {"start": v(-159.25, 8.85) * mm, "end": v(-159.25, 16.6) * mm});
            skArc(sketch, "E757", {"start": v(-162.25, -4.27) * mm, "mid": v(-160.75, -2.77) * mm, "end": v(-159.25, -4.27) * mm});
            skArc(sketch, "E758", {"start": v(-159.25, -4.27) * mm, "mid": v(-160.75, -5.77) * mm, "end": v(-162.25, -4.27) * mm});
            skLineSegment(sketch, "E759", {"start": v(-79.53, 115.6) * mm, "end": v(-79.53, 91.13) * mm});
            skLineSegment(sketch, "E760", {"start": v(-79.53, 91.13) * mm, "end": v(-79.53, 115.6) * mm});
            skLineSegment(sketch, "E761", {"start": v(158.03, 115.6) * mm, "end": v(158.03, 91.63) * mm});
            skLineSegment(sketch, "E762", {"start": v(158.03, 91.63) * mm, "end": v(158.03, 115.6) * mm});
            skLineSegment(sketch, "E763", {"start": v(39.25, 108.73) * mm, "end": v(-79.53, 108.73) * mm});
            skLineSegment(sketch, "E764", {"start": v(39.25, 108.73) * mm, "end": v(158.03, 108.73) * mm});
            skLineSegment(sketch, "E765", {"start": v(-103.13, -96.47) * mm, "end": v(-66.68, -96.47) * mm});
            skLineSegment(sketch, "E766", {"start": v(-66.68, -96.47) * mm, "end": v(-103.13, -96.47) * mm});
            skLineSegment(sketch, "E767", {"start": v(-103.13, 96.47) * mm, "end": v(-58.65, 96.47) * mm});
            skLineSegment(sketch, "E768", {"start": v(-58.65, 96.47) * mm, "end": v(-103.13, 96.47) * mm});
            skLineSegment(sketch, "E769", {"start": v(-96.26, 0) * mm, "end": v(-96.26, -96.47) * mm});
            skLineSegment(sketch, "E770", {"start": v(-96.26, 0) * mm, "end": v(-96.26, 96.47) * mm});
            const initialGuessF0  = {"E69": [-0.07902238100000002, 0.09116168, -0.495082, 0.100168, 0.000505114, 0.0005, -1.193157, 0.197663], "E104": [0.169725375, -0.108945582, -0.999979, -0.006518, 0.001, 0.000123421, 1.715643, 3.088829], "E114": [0.169725375, 0.108945583, -0.999979, 0.006518, 0.001, 0.000123421, -3.088829, -1.715643], "E135": [0.14303217799999995, 0.114508917, -0.026667, -0.999644, 0.001, 0.00045350400000000003, -3.082837, -2.965917], "E136": [0.14303217799999995, 0.114508917, -0.026667, -0.999644, 0.001, 0.00045350400000000003, -2.965917, -1.909476], "E137": [0.141346143, 0.114559866, -0.034001, -0.999422, 0.001, 0.000544263, -3.079167, -1.930119], "E160": [-0.09122537500000001, 0.108945583, -0.999979, -0.006518, 0.001, 0.000123421, -1.425949, -0.052764], "E161": [-0.09040017400000001, 0.10992905600000001, -0.167246, 0.985915, 0.001, 0.000123028, 0.052761, 1.42561], "E185": [0.15916246799999997, 0.09129315499999999, -0.49995, -0.007099, 0.0005, 5.0253e-05, -1.705945, -0.140342], "E252": [0.008557907, -0.17406351, 869.019096, -153.231513, 0.882425117, 0.046182561999999996, 1.677446, 1.694307], "E253": [-0.13720209500000002, 0, 0, -882.484642, 0.882484642, 0.046185678, 1.446889, 1.694704], "E256": [0.043878177, 0, 0, 899.987865, 0.899987865, 0.125254102, 1.469127, 1.672466], "E257": [0.027974271999999984, -0.06394782900000001, -884.010721, 155.874941, 0.897648011, 0.046979267, 1.457695, 1.471577], "E297": [-0.053139072000000016, 0.096822915, 0.065937, -0.495633, 0.0005, 0.000313859, 0.067283, 1.854473], "E310": [0.13163907199999997, 0.096822915, -0.065937, -0.495633, 0.0005, 0.000313859, -1.854473, -0.067283], "E369": [0.143205161, 0.11448886199999998, -0.202305, -0.979323, 0.001, 0.000486387, -3.069903, -1.824166], "E371": [0.216504666, 0, 0, -881.504103, 0.881504103, 0.04613436, -1.694704, -1.446889], "E373": [0.03412925899999999, 0, 0, 899.487872, 0.899487872, 0.125184516, -1.672466, -1.469127], "E375": [-0.13800466700000003, 0, 0, 881.504103, 0.881504103, 0.04613436, -1.694704, -1.446889], "E378": [0.03462182199999998, 0, 0, -899.987865, 0.899987865, 0.125254102, 1.469127, 1.672466], "E379": [0.05052572699999999, 0.06394783000000001, 884.010721, -155.874941, 0.897648011, 0.046979267, 1.457695, 1.471577], "E380": [0.069942093, 0.17406351, -869.019096, 153.231513, 0.882425117, 0.046182561999999996, 1.677446, 1.694307], "E381": [0.215702095, 0, 0, 882.484642, 0.882484642, 0.046185678, 1.446889, 1.694704], "E388": [0.044370739999999985, 0, 0, -899.487872, 0.899487872, 0.125184516, -1.672466, -1.469127], "E391": [-0.07584541200000001, 0.112404762, 0.168128, -0.985765, 0.001, 0.000106302, -3.088934, -1.716085], "E393": [-0.06470516200000001, 0.11448886199999998, 0.202305, -0.979323, 0.001, 0.000486387, 1.824166, 3.069903], "E439": [-0.06470516200000001, -0.114488862, -0.202305, -0.979323, 0.001, 0.000486387, 0.071689, 1.317427], "E523": [0.16924725499999996, -0.10938234200000001, 1.53567, -1.28858, 0.002004675, 0.002, -0.696982, 0.696982], "E540": [0.12222795499999999, -0.115423514, -19, 0, 0.019, 0.000995748, 1.570796, 2.524156], "E542": [-0.043727956000000005, -0.115423514, -19, 0, 0.019, 0.000995748, 0.617437, 1.570796], "E560": [-0.09074725600000001, -0.10938234200000001, -1.53567, -1.28858, 0.002004675, 0.002, -0.696982, 0.696982], "E630": [-0.043727956000000005, 0.11542351500000002, 19, 0, 0.019, 0.000995748, 1.570796, 2.524156], "E632": [0.12222795499999999, 0.11542351500000002, 19.003862, 0, 0.019003862000000003, 0.00099595, 0.617293, 1.590957]};
            skSetInitialGuess(sketch, initialGuessF0);
            skSolve(sketch);
        }
        {
            var Q0;
            Q0=qCreatedBy(makeId("Top.planeOp"),FACE);
            var sketch = newSketch(context, id + "F1", { "sketchPlane" : qUnion([Q0])});
            skArc(sketch, "E771.0.0", {"start": v(129.75, -75.5) * mm, "mid": v(133.81, -74.4) * mm, "end": v(136.75, -71.37) * mm});
            skLineSegment(sketch, "E771.0.1", {"start": v(136.75, -71.37) * mm, "end": v(136.75, -63.63) * mm});
            skArc(sketch, "E771.0.2", {"start": v(136.75, -63.63) * mm, "mid": v(133.81, -60.6) * mm, "end": v(129.75, -59.5) * mm});
            skArc(sketch, "E771.0.4", {"start": v(129.75, -59.5) * mm, "mid": v(125.69, -60.6) * mm, "end": v(122.75, -63.63) * mm});
            skLineSegment(sketch, "E771.0.5", {"start": v(122.75, -63.63) * mm, "end": v(122.75, -71.37) * mm});
            skArc(sketch, "E771.0.6", {"start": v(122.75, -71.37) * mm, "mid": v(125.69, -74.4) * mm, "end": v(129.75, -75.5) * mm});
            skArc(sketch, "E772.0.0", {"start": v(-58.25, -67.5) * mm, "mid": v(-40.75, -85) * mm, "end": v(-23.25, -67.5) * mm});
            skArc(sketch, "E772.0.1", {"start": v(-23.25, -67.5) * mm, "mid": v(-40.75, -50) * mm, "end": v(-58.25, -67.5) * mm});
            skLineSegment(sketch, "E773.0", {"start": v(135.16, -70.44) * mm, "end": v(135.16, -64.56) * mm, "construction": true});
            skArc(sketch, "E773.1", {"start": v(129.75, -73.91) * mm, "mid": v(132.58, -73.25) * mm, "end": v(134.83, -71.4) * mm, "construction": true});
            skArc(sketch, "E773.3", {"start": v(129.75, -61.09) * mm, "mid": v(126.92, -61.75) * mm, "end": v(124.67, -63.6) * mm, "construction": true});
            skLineSegment(sketch, "E773.4", {"start": v(124.34, -64.56) * mm, "end": v(124.34, -70.44) * mm, "construction": true});
            skArc(sketch, "E773.5", {"start": v(134.83, -63.6) * mm, "mid": v(132.58, -61.75) * mm, "end": v(129.75, -61.09) * mm, "construction": true});
            skArc(sketch, "E773.6", {"start": v(124.67, -71.4) * mm, "mid": v(126.92, -73.25) * mm, "end": v(129.75, -73.91) * mm, "construction": true});
            skCircle(sketch, "E774", {"center": v(132.84, -61.88) * mm, "radius": 1.59 * mm, "construction": true});
            skArc(sketch, "E775.0", {"start": v(-24.84, -67.5) * mm, "mid": v(-40.75, -51.59) * mm, "end": v(-56.66, -67.5) * mm, "construction": true});
            skArc(sketch, "E775.1", {"start": v(-56.66, -67.5) * mm, "mid": v(-40.75, -83.41) * mm, "end": v(-24.84, -67.5) * mm, "construction": true});
            skArc(sketch, "E776.0", {"start": v(9.45, -67.5) * mm, "mid": v(-40.75, -17.3) * mm, "end": v(-90.95, -67.5) * mm});
            skArc(sketch, "E777.0", {"start": v(-90.95, -67.5) * mm, "mid": v(-40.75, -117.7) * mm, "end": v(9.45, -67.5) * mm});
            skLineSegment(sketch, "E778.0", {"start": v(-92.75, 116.42) * mm, "end": v(-92.75, -116.42) * mm});
            skLineSegment(sketch, "E779.0", {"start": v(171.25, -116.42) * mm, "end": v(-92.75, -116.42) * mm});
            skLineSegment(sketch, "E780.0", {"start": v(171.25, -116.42) * mm, "end": v(171.25, 116.42) * mm});
            skLineSegment(sketch, "E781.0", {"start": v(-92.75, 116.42) * mm, "end": v(171.25, 116.42) * mm});
            skPoint(sketch, "E782.orphan", {"position": v(-43.73, 116.42) * mm});
            skPoint(sketch, "E783.orphan", {"position": v(-92.75, 109.39) * mm});
            skPoint(sketch, "E784.orphan", {"position": v(121.84, 116.42) * mm});
            skPoint(sketch, "E785.orphan", {"position": v(171.25, 109.39) * mm});
            skPoint(sketch, "E786.orphan", {"position": v(-92.75, -109.39) * mm});
            skPoint(sketch, "E787.orphan", {"position": v(-43.73, -116.42) * mm});
            skPoint(sketch, "E788.orphan", {"position": v(171.25, -109.39) * mm});
            skLineSegment(sketch, "E789.0", {"start": v(-97.75, 121.42) * mm, "end": v(176.25, 121.42) * mm});
            skLineSegment(sketch, "E789.1", {"start": v(-97.75, 121.42) * mm, "end": v(-97.75, -121.42) * mm});
            skLineSegment(sketch, "E789.2", {"start": v(176.25, -121.42) * mm, "end": v(-97.75, -121.42) * mm});
            skLineSegment(sketch, "E789.3", {"start": v(176.25, -121.42) * mm, "end": v(176.25, 121.42) * mm});
            skPoint(sketch, "E790.visualSharp", {"position": v(135.16, -64.06) * mm});
            skArc(sketch, "E790.filletArc", {"start": v(135.16, -64.56) * mm, "mid": v(135.08, -64.05) * mm, "end": v(134.83, -63.6) * mm, "construction": true});
            skPoint(sketch, "E791.visualSharp", {"position": v(135.16, -70.94) * mm});
            skArc(sketch, "E791.filletArc", {"start": v(134.83, -71.4) * mm, "mid": v(135.08, -70.95) * mm, "end": v(135.16, -70.44) * mm, "construction": true});
            skPoint(sketch, "E792.visualSharp", {"position": v(124.34, -70.94) * mm});
            skArc(sketch, "E792.filletArc", {"start": v(124.34, -70.44) * mm, "mid": v(124.42, -70.95) * mm, "end": v(124.67, -71.4) * mm, "construction": true});
            skPoint(sketch, "E793.visualSharp", {"position": v(124.34, -64.06) * mm});
            skArc(sketch, "E793.filletArc", {"start": v(124.67, -63.6) * mm, "mid": v(124.42, -64.05) * mm, "end": v(124.34, -64.56) * mm, "construction": true});
            skArc(sketch, "E794.0", {"start": v(162.02, -42.69) * mm, "mid": v(147.73, -30.99) * mm, "end": v(129.75, -26.8) * mm});
            skArc(sketch, "E794.1", {"start": v(169.45, -64.56) * mm, "mid": v(167.54, -53) * mm, "end": v(162.02, -42.69) * mm});
            skArc(sketch, "E794.2", {"start": v(129.75, -26.8) * mm, "mid": v(111.77, -30.99) * mm, "end": v(97.48, -42.69) * mm});
            skLineSegment(sketch, "E794.3", {"start": v(169.45, -70.44) * mm, "end": v(169.45, -64.56) * mm});
            skArc(sketch, "E794.4", {"start": v(162.02, -92.31) * mm, "mid": v(167.54, -82) * mm, "end": v(169.45, -70.44) * mm});
            skArc(sketch, "E794.5", {"start": v(129.75, -108.2) * mm, "mid": v(147.73, -104.01) * mm, "end": v(162.02, -92.31) * mm});
            skArc(sketch, "E794.6", {"start": v(97.48, -42.69) * mm, "mid": v(91.96, -53) * mm, "end": v(90.05, -64.56) * mm});
            skLineSegment(sketch, "E794.7", {"start": v(90.05, -64.56) * mm, "end": v(90.05, -70.44) * mm});
            skArc(sketch, "E794.8", {"start": v(90.05, -70.44) * mm, "mid": v(91.96, -82) * mm, "end": v(97.48, -92.31) * mm});
            skArc(sketch, "E794.9", {"start": v(97.48, -92.31) * mm, "mid": v(111.77, -104.01) * mm, "end": v(129.75, -108.2) * mm});
            skSolve(sketch);
        }
        {
            var Q0;
            {var subQ6=sQuery(id+"F1.wireOp",EDGE,"E776.0");Q0=makeQuery(id+"F1.imprint","IMPRINT",FACE,{"disambiguationData":[TD([[makeQuery(id+"F1.imprint","IMPRINT",EDGE,{"derivedFrom":subQ6}),-1.0]])]});}
            var Q1;
            {var subQ4=sQuery(id+"F1.wireOp",EDGE,"E778.0");Q1=makeQuery(id+"F1.imprint","IMPRINT",FACE,{"disambiguationData":[TD([[makeQuery(id+"F1.imprint","IMPRINT",EDGE,{"derivedFrom":subQ4}),-1.0]])]});}
            extrude(context, id + "F2", {"entities" : qUnion([Q0, Q1]), "depth" : 5 * mm, "offsetDistance" : 25 * mm});
        }
        {
            var Q0;
            {var subQ4=sQuery(id+"F1.wireOp",EDGE,"E778.0");Q0=makeQuery(id+"F1.imprint","IMPRINT",FACE,{"disambiguationData":[TD([[makeQuery(id+"F1.imprint","IMPRINT",EDGE,{"derivedFrom":subQ4}),-1.0]])]});}
            extrude(context, id + "F3", {"entities" : qUnion([Q0]), "operationType" : NewBodyOperationType.ADD, "oppositeDirection" : true, "depth" : 15 * mm, "offsetDistance" : 25 * mm});
        }
    });
